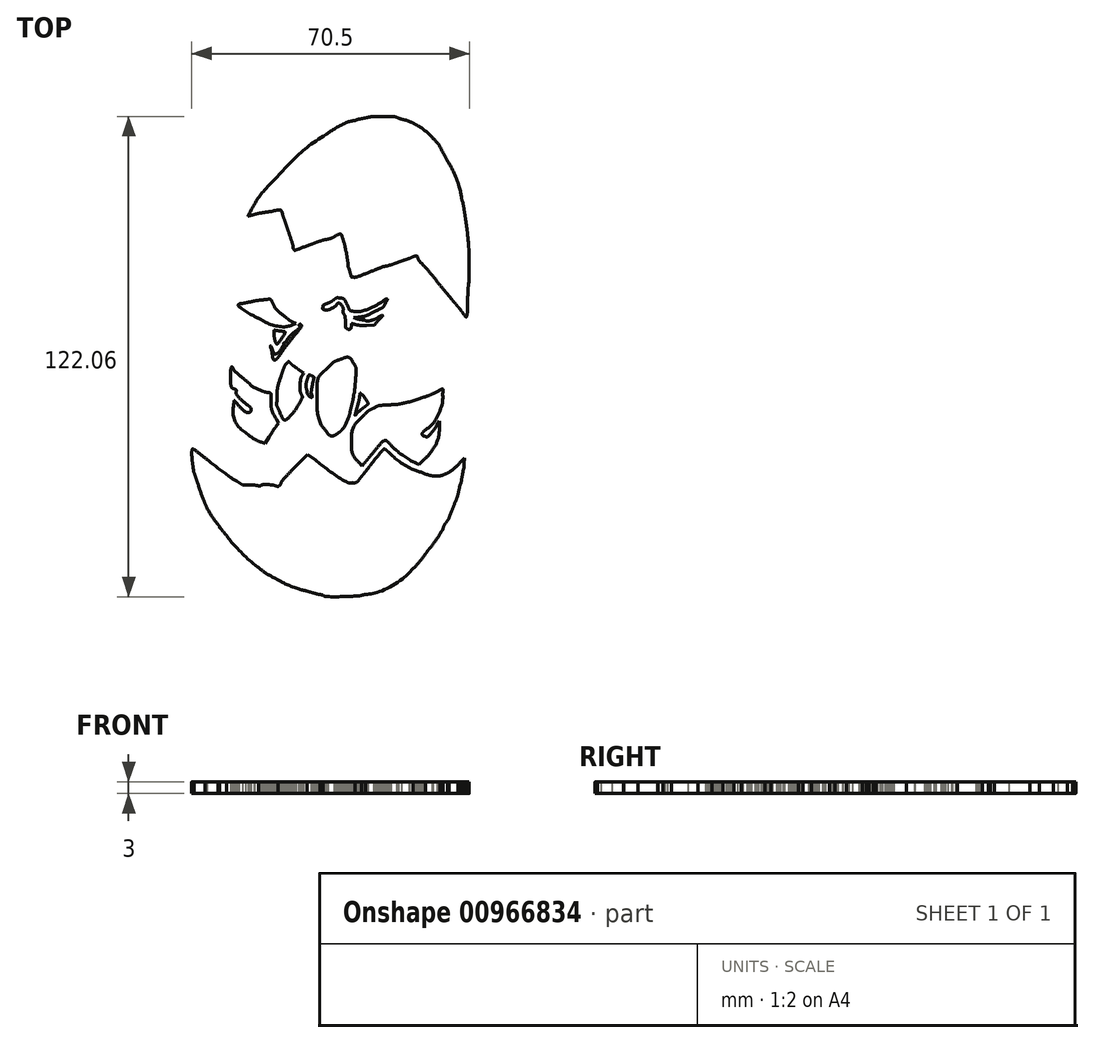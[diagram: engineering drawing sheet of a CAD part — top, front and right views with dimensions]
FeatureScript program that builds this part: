
annotation { "Feature Type Name" : "Feature", "Feature Type Description" : "" }
export const myFeature = defineFeature(function(context is Context, id is Id, definition is map)
    precondition{}
    {
        {
            var Q0;
            Q0=qCreatedBy(makeId("Top.planeOp"),FACE);
            var sketch = newSketch(context, id + "F0", { "sketchPlane" : qUnion([Q0])});
            skLineSegment(sketch, "E0", {"start": v(-17.64, -24.34) * mm, "end": v(-17.4, -23.74) * mm});
            skLineSegment(sketch, "E1", {"start": v(-17.4, -23.74) * mm, "end": v(-18.32, -23.36) * mm});
            skLineSegment(sketch, "E2", {"start": v(-18.63, 27.42) * mm, "end": v(-17.84, 26.76) * mm});
            skLineSegment(sketch, "E3", {"start": v(-17.84, 26.76) * mm, "end": v(-16.9, 28.16) * mm});
            skLineSegment(sketch, "E4", {"start": v(1.09, -62.5) * mm, "end": v(1.09, -62.5) * mm});
            skLineSegment(sketch, "E5", {"start": v(34.01, -27.2) * mm, "end": v(34.13, -25.85) * mm});
            skLineSegment(sketch, "E6", {"start": v(34.13, -25.85) * mm, "end": v(33.12, -26.87) * mm});
            skLineSegment(sketch, "E7", {"start": v(-3.82, -26.37) * mm, "end": v(-5.8, -24.88) * mm});
            skLineSegment(sketch, "E8", {"start": v(-5.8, -24.88) * mm, "end": v(-9, -28.14) * mm});
            skLineSegment(sketch, "E9", {"start": v(-20.55, -32.7) * mm, "end": v(-22.26, -32.68) * mm});
            skLineSegment(sketch, "E10", {"start": v(-22.26, -32.68) * mm, "end": v(-23.8, -31.71) * mm});
            skLineSegment(sketch, "E11", {"start": v(-17.33, -29.73) * mm, "end": v(-17.41, -31.05) * mm});
            skLineSegment(sketch, "E12", {"start": v(-17.41, -31.05) * mm, "end": v(-16.23, -31.1) * mm});
            skLineSegment(sketch, "E13", {"start": v(21.94, -27.16) * mm, "end": v(22.57, -27.45) * mm});
            skLineSegment(sketch, "E14", {"start": v(22.57, -27.45) * mm, "end": v(23.83, -26.21) * mm});
            skLineSegment(sketch, "E15", {"start": v(27.7, -17.94) * mm, "end": v(27.78, -16.4) * mm});
            skLineSegment(sketch, "E16", {"start": v(27.78, -16.4) * mm, "end": v(27.08, -17.43) * mm});
            skLineSegment(sketch, "E17", {"start": v(7.35, -27.02) * mm, "end": v(8.09, -27.86) * mm});
            skLineSegment(sketch, "E18", {"start": v(8.09, -27.86) * mm, "end": v(8.6, -27.2) * mm});
            skLineSegment(sketch, "E19", {"start": v(-13.84, -17.87) * mm, "end": v(-13.14, -16.9) * mm});
            skLineSegment(sketch, "E20", {"start": v(-13.14, -16.9) * mm, "end": v(-13.63, -16.05) * mm});
            skLineSegment(sketch, "E21", {"start": v(-17.2, -21.9) * mm, "end": v(-16.6, -22.1) * mm});
            skLineSegment(sketch, "E22", {"start": v(-16.6, -22.1) * mm, "end": v(-15.58, -20.48) * mm});
            skLineSegment(sketch, "E23", {"start": v(-7, -4.65) * mm, "end": v(-6.75, -4.17) * mm});
            skLineSegment(sketch, "E24", {"start": v(-6.75, -4.17) * mm, "end": v(-8.1, -3.28) * mm});
            skLineSegment(sketch, "E25", {"start": v(29.2, 13.04) * mm, "end": v(29.43, 13.93) * mm});
            skLineSegment(sketch, "E26", {"start": v(29.43, 13.93) * mm, "end": v(28.41, 15.23) * mm});
            skLineSegment(sketch, "E27", {"start": v(1.96, 28.65) * mm, "end": v(1.77, 29.1) * mm});
            skLineSegment(sketch, "E28", {"start": v(1.77, 29.1) * mm, "end": v(0.99, 28.8) * mm});
            skLineSegment(sketch, "E29", {"start": v(-14.89, 28.54) * mm, "end": v(-16.04, 27) * mm});
            skLineSegment(sketch, "E30", {"start": v(-16.04, 27) * mm, "end": v(-15.46, 26.94) * mm});
            skLineSegment(sketch, "E31", {"start": v(-4.31, -3.35) * mm, "end": v(-3.52, -3.65) * mm});
            skLineSegment(sketch, "E32", {"start": v(-3.52, -3.65) * mm, "end": v(-1.91, -2.03) * mm});
            skLineSegment(sketch, "E33", {"start": v(10.44, -4.22) * mm, "end": v(10.44, -4.22) * mm});
            skLineSegment(sketch, "E34", {"start": v(7.03, 10) * mm, "end": v(5.92, 9.88) * mm});
            skLineSegment(sketch, "E35", {"start": v(5.92, 9.88) * mm, "end": v(6.58, 9.65) * mm});
            skLineSegment(sketch, "E36", {"start": v(11.62, 8.44) * mm, "end": v(11.2, 7.9) * mm});
            skLineSegment(sketch, "E37", {"start": v(11.2, 7.9) * mm, "end": v(9.22, 7.89) * mm});
            skLineSegment(sketch, "E38", {"start": v(-9.5, 8.1) * mm, "end": v(-8.74, 8.33) * mm});
            skLineSegment(sketch, "E39", {"start": v(-8.74, 8.33) * mm, "end": v(-9.55, 8.72) * mm});
            skFitSpline(sketch, "E40", {"points": [v(1.09, -62.5) * mm, v(1.07, -62.49) * mm, v(0.46, -62.46) * mm, v(-0.26, -62.44) * mm]});
            skFitSpline(sketch, "E41", {"points": [v(-0.26, -62.44) * mm, v(-1.46, -62.4) * mm, v(-3.84, -62.05) * mm, v(-4.15, -61.86) * mm]});
            skFitSpline(sketch, "E42", {"points": [v(-4.15, -61.86) * mm, v(-4.22, -61.82) * mm, v(-4.46, -61.75) * mm, v(-4.7, -61.7) * mm]});
            skFitSpline(sketch, "E43", {"points": [v(-4.7, -61.7) * mm, v(-4.92, -61.66) * mm, v(-5.61, -61.47) * mm, v(-6.23, -61.27) * mm]});
            skFitSpline(sketch, "E44", {"points": [v(-6.23, -61.27) * mm, v(-6.84, -61.07) * mm, v(-7.52, -60.87) * mm, v(-7.74, -60.83) * mm]});
            skFitSpline(sketch, "E45", {"points": [v(-7.74, -60.83) * mm, v(-8.13, -60.75) * mm, v(-9.97, -60.15) * mm, v(-10.6, -59.88) * mm]});
            skFitSpline(sketch, "E46", {"points": [v(-10.6, -59.88) * mm, v(-10.79, -59.8) * mm, v(-11.21, -59.65) * mm, v(-11.54, -59.53) * mm]});
            skFitSpline(sketch, "E47", {"points": [v(-11.54, -59.53) * mm, v(-12.86, -59.06) * mm, v(-16.51, -57.07) * mm, v(-17.91, -56.06) * mm]});
            skFitSpline(sketch, "E48", {"points": [v(-17.91, -56.06) * mm, v(-20.14, -54.45) * mm, v(-20.57, -54.07) * mm, v(-23.72, -50.89) * mm]});
            skFitSpline(sketch, "E49", {"points": [v(-23.72, -50.89) * mm, v(-26.76, -47.82) * mm, v(-27.5, -47.02) * mm, v(-27.5, -46.8) * mm]});
            skFitSpline(sketch, "E50", {"points": [v(-27.5, -46.8) * mm, v(-27.5, -46.71) * mm, v(-27.87, -46.25) * mm, v(-28.33, -45.76) * mm]});
            skFitSpline(sketch, "E51", {"points": [v(-28.33, -45.76) * mm, v(-29.79, -44.22) * mm, v(-32.43, -40.02) * mm, v(-33.48, -37.57) * mm]});
            skFitSpline(sketch, "E52", {"points": [v(-33.48, -37.57) * mm, v(-33.92, -36.56) * mm, v(-34.68, -34.57) * mm, v(-34.78, -34.15) * mm]});
            skFitSpline(sketch, "E53", {"points": [v(-34.78, -34.15) * mm, v(-34.82, -34) * mm, v(-35.05, -33.32) * mm, v(-35.3, -32.6) * mm]});
            skFitSpline(sketch, "E54", {"points": [v(-35.3, -32.6) * mm, v(-36.32, -29.73) * mm, v(-36.5, -28.65) * mm, v(-36.5, -25.32) * mm]});
            skFitSpline(sketch, "E55", {"points": [v(-36.5, -25.32) * mm, v(-36.5, -22.53) * mm, v(-36.34, -21.27) * mm, v(-35.96, -21) * mm]});
            skFitSpline(sketch, "E56", {"points": [v(-35.96, -21) * mm, v(-35.54, -20.68) * mm, v(-35.42, -20.71) * mm, v(-34.9, -21.26) * mm]});
            skFitSpline(sketch, "E57", {"points": [v(-34.9, -21.26) * mm, v(-34.65, -21.52) * mm, v(-33.59, -22.39) * mm, v(-32.55, -23.18) * mm]});
            skFitSpline(sketch, "E58", {"points": [v(-32.55, -23.18) * mm, v(-31.51, -23.97) * mm, v(-30.63, -24.66) * mm, v(-30.58, -24.71) * mm]});
            skFitSpline(sketch, "E59", {"points": [v(-30.58, -24.71) * mm, v(-30.53, -24.76) * mm, v(-30.19, -25.03) * mm, v(-29.8, -25.3) * mm]});
            skFitSpline(sketch, "E60", {"points": [v(-29.8, -25.3) * mm, v(-29.43, -25.59) * mm, v(-29.08, -25.86) * mm, v(-29.04, -25.92) * mm]});
            skFitSpline(sketch, "E61", {"points": [v(-29.04, -25.92) * mm, v(-28.68, -26.36) * mm, v(-24.52, -29.29) * mm, v(-22.01, -30.85) * mm]});
            skFitSpline(sketch, "E62", {"points": [v(-22.01, -30.85) * mm, v(-21.6, -31.12) * mm, v(-19.15, -31.3) * mm, v(-19.01, -31.08) * mm]});
            skFitSpline(sketch, "E63", {"points": [v(-19.01, -31.08) * mm, v(-18.98, -31.02) * mm, v(-18.9, -30.43) * mm, v(-18.84, -29.77) * mm]});
            skFitSpline(sketch, "E64", {"points": [v(-18.84, -29.77) * mm, v(-18.78, -29.12) * mm, v(-18.7, -28.46) * mm, v(-18.66, -28.32) * mm]});
            skFitSpline(sketch, "E65", {"points": [v(-18.66, -28.32) * mm, v(-18.62, -28.18) * mm, v(-18.54, -27.8) * mm, v(-18.49, -27.46) * mm]});
            skFitSpline(sketch, "E66", {"points": [v(-18.49, -27.46) * mm, v(-18.33, -26.53) * mm, v(-17.92, -25) * mm, v(-17.64, -24.34) * mm]});
            skFitSpline(sketch, "E67", {"points": [v(-18.32, -23.36) * mm, v(-19.44, -22.9) * mm, v(-21.28, -21.62) * mm, v(-22.38, -20.55) * mm]});
            skFitSpline(sketch, "E68", {"points": [v(-22.38, -20.55) * mm, v(-24.7, -18.28) * mm, v(-26.1, -14.85) * mm, v(-25.9, -11.94) * mm]});
            skFitSpline(sketch, "E69", {"points": [v(-25.9, -11.94) * mm, v(-25.84, -11.19) * mm, v(-25.75, -10.37) * mm, v(-25.7, -10.14) * mm]});
            skFitSpline(sketch, "E70", {"points": [v(-25.7, -10.14) * mm, v(-25.64, -9.86) * mm, v(-25.76, -9.39) * mm, v(-26.08, -8.77) * mm]});
            skFitSpline(sketch, "E71", {"points": [v(-26.08, -8.77) * mm, v(-26.54, -7.84) * mm, v(-26.55, -7.77) * mm, v(-26.52, -4.97) * mm]});
            skFitSpline(sketch, "E72", {"points": [v(-26.52, -4.97) * mm, v(-26.5, -2.23) * mm, v(-26.48, -2.09) * mm, v(-26, -1.08) * mm]});
            skFitSpline(sketch, "E73", {"points": [v(-26, -1.08) * mm, v(-25.5, 0.03) * mm, v(-25.26, 0.23) * mm, v(-24.7, 0.05) * mm]});
            skFitSpline(sketch, "E74", {"points": [v(-24.7, 0.05) * mm, v(-24.38, -0.05) * mm, v(-23.44, -1.82) * mm, v(-23.53, -2.16) * mm]});
            skFitSpline(sketch, "E75", {"points": [v(-23.53, -2.16) * mm, v(-23.56, -2.26) * mm, v(-23.52, -2.28) * mm, v(-23.46, -2.22) * mm]});
            skFitSpline(sketch, "E76", {"points": [v(-23.46, -2.22) * mm, v(-23.4, -2.15) * mm, v(-23.1, -2.39) * mm, v(-22.8, -2.73) * mm]});
            skFitSpline(sketch, "E77", {"points": [v(-22.8, -2.73) * mm, v(-21.53, -4.2) * mm, v(-20.04, -5.4) * mm, v(-18.23, -6.4) * mm]});
            skFitSpline(sketch, "E78", {"points": [v(-18.23, -6.4) * mm, v(-17.03, -7.06) * mm, v(-14.86, -7.85) * mm, v(-14.69, -7.68) * mm]});
            skFitSpline(sketch, "E79", {"points": [v(-14.69, -7.68) * mm, v(-14.63, -7.63) * mm, v(-14.52, -7.22) * mm, v(-14.44, -6.77) * mm]});
            skFitSpline(sketch, "E80", {"points": [v(-14.44, -6.77) * mm, v(-14.35, -6.33) * mm, v(-13.98, -5.12) * mm, v(-13.6, -4.1) * mm]});
            skFitSpline(sketch, "E81", {"points": [v(-13.6, -4.1) * mm, v(-13.22, -3.06) * mm, v(-12.91, -2.19) * mm, v(-12.91, -2.14) * mm]});
            skFitSpline(sketch, "E82", {"points": [v(-12.91, -2.14) * mm, v(-12.91, -2.1) * mm, v(-13.06, -2.15) * mm, v(-13.25, -2.24) * mm]});
            skFitSpline(sketch, "E83", {"points": [v(-13.25, -2.24) * mm, v(-13.7, -2.49) * mm, v(-14.83, -2.46) * mm, v(-15.18, -2.18) * mm]});
            skFitSpline(sketch, "E84", {"points": [v(-15.18, -2.18) * mm, v(-15.57, -1.9) * mm, v(-15.94, -1) * mm, v(-16.09, -0.02) * mm]});
            skFitSpline(sketch, "E85", {"points": [v(-16.09, -0.02) * mm, v(-16.15, 0.4) * mm, v(-16.26, 0.86) * mm, v(-16.33, 1) * mm]});
            skFitSpline(sketch, "E86", {"points": [v(-16.33, 1) * mm, v(-16.45, 1.24) * mm, v(-16.58, 1.76) * mm, v(-16.8, 2.98) * mm]});
            skFitSpline(sketch, "E87", {"points": [v(-16.8, 2.98) * mm, v(-16.84, 3.17) * mm, v(-16.94, 3.6) * mm, v(-17.03, 3.93) * mm]});
            skFitSpline(sketch, "E88", {"points": [v(-17.03, 3.93) * mm, v(-17.11, 4.26) * mm, v(-17.23, 4.91) * mm, v(-17.28, 5.38) * mm]});
            skFitSpline(sketch, "E89", {"points": [v(-17.28, 5.38) * mm, v(-17.52, 7.42) * mm, v(-17.6, 7.56) * mm, v(-19.14, 8.38) * mm]});
            skFitSpline(sketch, "E90", {"points": [v(-19.14, 8.38) * mm, v(-21.39, 9.58) * mm, v(-22.76, 10.52) * mm, v(-23.65, 11.48) * mm]});
            skFitSpline(sketch, "E91", {"points": [v(-23.65, 11.48) * mm, v(-24.11, 11.97) * mm, v(-24.74, 12.6) * mm, v(-25.05, 12.9) * mm]});
            skFitSpline(sketch, "E92", {"points": [v(-25.05, 12.9) * mm, v(-25.6, 13.41) * mm, v(-25.74, 13.91) * mm, v(-25.46, 14.35) * mm]});
            skFitSpline(sketch, "E93", {"points": [v(-25.46, 14.35) * mm, v(-25.39, 14.46) * mm, v(-24.68, 14.64) * mm, v(-23.88, 14.73) * mm]});
            skFitSpline(sketch, "E94", {"points": [v(-23.88, 14.73) * mm, v(-20.97, 15.08) * mm, v(-20.33, 15.2) * mm, v(-20.16, 15.48) * mm]});
            skFitSpline(sketch, "E95", {"points": [v(-20.16, 15.48) * mm, v(-20.1, 15.59) * mm, v(-20.03, 16.45) * mm, v(-20.02, 17.39) * mm]});
            skFitSpline(sketch, "E96", {"points": [v(-20.02, 17.39) * mm, v(-20.01, 18.33) * mm, v(-19.94, 19.41) * mm, v(-19.87, 19.8) * mm]});
            skFitSpline(sketch, "E97", {"points": [v(-19.87, 19.8) * mm, v(-19.7, 20.59) * mm, v(-19.65, 20.93) * mm, v(-19.52, 21.8) * mm]});
            skFitSpline(sketch, "E98", {"points": [v(-19.52, 21.8) * mm, v(-19.47, 22.16) * mm, v(-19.27, 22.84) * mm, v(-19.08, 23.33) * mm]});
            skFitSpline(sketch, "E99", {"points": [v(-19.08, 23.33) * mm, v(-18.89, 23.81) * mm, v(-18.76, 24.24) * mm, v(-18.8, 24.28) * mm]});
            skFitSpline(sketch, "E100", {"points": [v(-18.8, 24.28) * mm, v(-18.84, 24.32) * mm, v(-19.05, 24.38) * mm, v(-19.28, 24.42) * mm]});
            skFitSpline(sketch, "E101", {"points": [v(-19.28, 24.42) * mm, v(-20.48, 24.65) * mm, v(-20.79, 24.73) * mm, v(-21.54, 24.97) * mm]});
            skFitSpline(sketch, "E102", {"points": [v(-21.54, 24.97) * mm, v(-22.34, 25.22) * mm, v(-22.36, 25.24) * mm, v(-22.31, 25.85) * mm]});
            skFitSpline(sketch, "E103", {"points": [v(-22.31, 25.85) * mm, v(-22.27, 26.4) * mm, v(-22.2, 26.48) * mm, v(-21.83, 26.48) * mm]});
            skFitSpline(sketch, "E104", {"points": [v(-21.83, 26.48) * mm, v(-21.6, 26.47) * mm, v(-21.03, 26.37) * mm, v(-20.58, 26.24) * mm]});
            skFitSpline(sketch, "E105", {"points": [v(-20.58, 26.24) * mm, v(-19.65, 25.97) * mm, v(-19.39, 26.08) * mm, v(-19.89, 26.52) * mm]});
            skFitSpline(sketch, "E106", {"points": [v(-19.89, 26.52) * mm, v(-20.48, 27.04) * mm, v(-21.49, 28.46) * mm, v(-21.49, 28.78) * mm]});
            skFitSpline(sketch, "E107", {"points": [v(-21.49, 28.78) * mm, v(-21.49, 28.94) * mm, v(-21.38, 29.22) * mm, v(-21.24, 29.4) * mm]});
            skFitSpline(sketch, "E108", {"points": [v(-21.24, 29.4) * mm, v(-21, 29.73) * mm, v(-20.96, 29.7) * mm, v(-20.2, 28.9) * mm]});
            skFitSpline(sketch, "E109", {"points": [v(-20.2, 28.9) * mm, v(-19.78, 28.45) * mm, v(-19.07, 27.78) * mm, v(-18.63, 27.42) * mm]});
            skFitSpline(sketch, "E110", {"points": [v(-16.9, 28.16) * mm, v(-15.9, 29.64) * mm, v(-14.7, 31.14) * mm, v(-13.47, 32.36) * mm]});
            skFitSpline(sketch, "E111", {"points": [v(-13.47, 32.36) * mm, v(-13.07, 32.77) * mm, v(-12.74, 33.2) * mm, v(-12.74, 33.33) * mm]});
            skFitSpline(sketch, "E112", {"points": [v(-12.74, 33.33) * mm, v(-12.74, 33.45) * mm, v(-12.94, 34) * mm, v(-13.18, 34.54) * mm]});
            skFitSpline(sketch, "E113", {"points": [v(-13.18, 34.54) * mm, v(-13.6, 35.5) * mm, v(-13.63, 35.52) * mm, v(-14.16, 35.42) * mm]});
            skFitSpline(sketch, "E114", {"points": [v(-14.16, 35.42) * mm, v(-14.47, 35.36) * mm, v(-15.06, 35.27) * mm, v(-15.49, 35.21) * mm]});
            skFitSpline(sketch, "E115", {"points": [v(-15.49, 35.21) * mm, v(-17.01, 35.02) * mm, v(-19.02, 34.64) * mm, v(-19.86, 34.39) * mm]});
            skFitSpline(sketch, "E116", {"points": [v(-19.86, 34.39) * mm, v(-20.33, 34.25) * mm, v(-20.98, 34.1) * mm, v(-21.3, 34.05) * mm]});
            skFitSpline(sketch, "E117", {"points": [v(-21.3, 34.05) * mm, v(-21.62, 34) * mm, v(-21.96, 33.88) * mm, v(-22.06, 33.78) * mm]});
            skFitSpline(sketch, "E118", {"points": [v(-22.06, 33.78) * mm, v(-22.16, 33.68) * mm, v(-22.41, 33.6) * mm, v(-22.62, 33.6) * mm]});
            skFitSpline(sketch, "E119", {"points": [v(-22.62, 33.6) * mm, v(-23.45, 33.6) * mm, v(-23.52, 34.51) * mm, v(-22.77, 35.72) * mm]});
            skFitSpline(sketch, "E120", {"points": [v(-22.77, 35.72) * mm, v(-19.1, 41.6) * mm, v(-18.03, 43.06) * mm, v(-15.74, 45.35) * mm]});
            skFitSpline(sketch, "E121", {"points": [v(-15.74, 45.35) * mm, v(-11.87, 49.2) * mm, v(-7.67, 53.23) * mm, v(-6.65, 54.1) * mm]});
            skFitSpline(sketch, "E122", {"points": [v(-6.65, 54.1) * mm, v(-6.09, 54.57) * mm, v(-5.48, 55.09) * mm, v(-5.3, 55.25) * mm]});
            skFitSpline(sketch, "E123", {"points": [v(-5.3, 55.25) * mm, v(-5.12, 55.41) * mm, v(-4.65, 55.76) * mm, v(-4.27, 56.02) * mm]});
            skFitSpline(sketch, "E124", {"points": [v(-4.27, 56.02) * mm, v(-3.88, 56.28) * mm, v(-3.53, 56.54) * mm, v(-3.48, 56.6) * mm]});
            skFitSpline(sketch, "E125", {"points": [v(-3.48, 56.6) * mm, v(-3.18, 56.94) * mm, v(-0.95, 58.3) * mm, v(1, 59.31) * mm]});
            skFitSpline(sketch, "E126", {"points": [v(1, 59.31) * mm, v(3, 60.36) * mm, v(6, 61.53) * mm, v(7.33, 61.8) * mm]});
            skFitSpline(sketch, "E127", {"points": [v(7.33, 61.8) * mm, v(10.1, 62.34) * mm, v(10.94, 62.44) * mm, v(13.33, 62.5) * mm]});
            skFitSpline(sketch, "E128", {"points": [v(13.33, 62.5) * mm, v(15.91, 62.56) * mm, v(17.13, 62.4) * mm, v(19.1, 61.74) * mm]});
            skFitSpline(sketch, "E129", {"points": [v(19.1, 61.74) * mm, v(22.69, 60.54) * mm, v(26.05, 58.26) * mm, v(27.97, 55.74) * mm]});
            skFitSpline(sketch, "E130", {"points": [v(27.97, 55.74) * mm, v(29.06, 54.31) * mm, v(30.31, 52.15) * mm, v(31.72, 49.27) * mm]});
            skFitSpline(sketch, "E131", {"points": [v(31.72, 49.27) * mm, v(33.14, 46.38) * mm, v(33.63, 45.02) * mm, v(34.5, 41.57) * mm]});
            skFitSpline(sketch, "E132", {"points": [v(34.5, 41.57) * mm, v(35.22, 38.77) * mm, v(35.23, 38.75) * mm, v(35.54, 36.43) * mm]});
            skFitSpline(sketch, "E133", {"points": [v(35.54, 36.43) * mm, v(35.58, 36.15) * mm, v(35.64, 35.76) * mm, v(35.68, 35.57) * mm]});
            skFitSpline(sketch, "E134", {"points": [v(35.68, 35.57) * mm, v(35.73, 35.38) * mm, v(35.81, 34.65) * mm, v(35.88, 33.94) * mm]});
            skFitSpline(sketch, "E135", {"points": [v(35.88, 33.94) * mm, v(35.94, 33.23) * mm, v(36.02, 32.46) * mm, v(36.05, 32.23) * mm]});
            skFitSpline(sketch, "E136", {"points": [v(36.05, 32.23) * mm, v(36.24, 30.91) * mm, v(36.36, 29.83) * mm, v(36.41, 29.06) * mm]});
            skFitSpline(sketch, "E137", {"points": [v(36.41, 29.06) * mm, v(36.5, 27.7) * mm, v(36.5, 19.13) * mm, v(36.4, 17.22) * mm]});
            skFitSpline(sketch, "E138", {"points": [v(36.4, 17.22) * mm, v(36.35, 16.27) * mm, v(36.28, 14.54) * mm, v(36.24, 13.36) * mm]});
            skFitSpline(sketch, "E139", {"points": [v(36.24, 13.36) * mm, v(36.2, 12.18) * mm, v(36.14, 10.94) * mm, v(36.08, 10.61) * mm]});
            skFitSpline(sketch, "E140", {"points": [v(36.08, 10.61) * mm, v(36.03, 10.28) * mm, v(35.97, 9.42) * mm, v(35.95, 8.7) * mm]});
            skFitSpline(sketch, "E141", {"points": [v(35.95, 8.7) * mm, v(35.9, 7.22) * mm, v(35.76, 7.03) * mm, v(34.78, 7.16) * mm]});
            skFitSpline(sketch, "E142", {"points": [v(34.78, 7.16) * mm, v(34.69, 7.18) * mm, v(34.36, 7.55) * mm, v(34.06, 8) * mm]});
            skFitSpline(sketch, "E143", {"points": [v(34.06, 8) * mm, v(33.1, 9.4) * mm, v(30.96, 12.07) * mm, v(30.76, 12.1) * mm]});
            skFitSpline(sketch, "E144", {"points": [v(30.76, 12.1) * mm, v(30.65, 12.13) * mm, v(30.27, 11.52) * mm, v(29.9, 10.75) * mm]});
            skFitSpline(sketch, "E145", {"points": [v(29.9, 10.75) * mm, v(29.33, 9.57) * mm, v(27.59, 6.78) * mm, v(27.24, 6.5) * mm]});
            skFitSpline(sketch, "E146", {"points": [v(27.24, 6.5) * mm, v(27.18, 6.45) * mm, v(26.87, 6.07) * mm, v(26.54, 5.64) * mm]});
            skFitSpline(sketch, "E147", {"points": [v(26.54, 5.64) * mm, v(24.96, 3.59) * mm, v(21.88, 0.6) * mm, v(19.59, -1.12) * mm]});
            skFitSpline(sketch, "E148", {"points": [v(19.59, -1.12) * mm, v(15.64, -4.08) * mm, v(12.52, -5.52) * mm, v(8.8, -6.1) * mm]});
            skFitSpline(sketch, "E149", {"points": [v(8.8, -6.1) * mm, v(7.97, -6.23) * mm, v(7.9, -6.27) * mm, v(7.8, -6.78) * mm]});
            skFitSpline(sketch, "E150", {"points": [v(7.8, -6.78) * mm, v(7.74, -7.1) * mm, v(7.92, -7.38) * mm, v(8.65, -8.1) * mm]});
            skFitSpline(sketch, "E151", {"points": [v(8.65, -8.1) * mm, v(9.16, -8.6) * mm, v(9.93, -9.54) * mm, v(10.36, -10.18) * mm]});
            skFitSpline(sketch, "E152", {"points": [v(10.36, -10.18) * mm, v(11.19, -11.43) * mm, v(11.13, -11.4) * mm, v(12.47, -11.1) * mm]});
            skFitSpline(sketch, "E153", {"points": [v(12.47, -11.1) * mm, v(12.7, -11.06) * mm, v(13.71, -10.97) * mm, v(14.7, -10.91) * mm]});
            skFitSpline(sketch, "E154", {"points": [v(14.7, -10.91) * mm, v(15.7, -10.86) * mm, v(16.7, -10.79) * mm, v(16.93, -10.76) * mm]});
            skFitSpline(sketch, "E155", {"points": [v(16.93, -10.76) * mm, v(18.33, -10.57) * mm, v(19.12, -10.42) * mm, v(19.5, -10.27) * mm]});
            skFitSpline(sketch, "E156", {"points": [v(19.5, -10.27) * mm, v(19.74, -10.18) * mm, v(20.05, -10.08) * mm, v(20.19, -10.05) * mm]});
            skFitSpline(sketch, "E157", {"points": [v(20.19, -10.05) * mm, v(20.67, -9.95) * mm, v(24.21, -8.65) * mm, v(25.5, -8.1) * mm]});
            skFitSpline(sketch, "E158", {"points": [v(25.5, -8.1) * mm, v(26.21, -7.8) * mm, v(27.32, -7.22) * mm, v(27.97, -6.8) * mm]});
            skFitSpline(sketch, "E159", {"points": [v(27.97, -6.8) * mm, v(29, -6.14) * mm, v(29.2, -6.07) * mm, v(29.56, -6.24) * mm]});
            skFitSpline(sketch, "E160", {"points": [v(29.56, -6.24) * mm, v(30.1, -6.48) * mm, v(30.2, -6.94) * mm, v(30.1, -8.74) * mm]});
            skFitSpline(sketch, "E161", {"points": [v(30.1, -8.74) * mm, v(30, -10.44) * mm, v(30.06, -10.14) * mm, v(29.27, -12.55) * mm]});
            skFitSpline(sketch, "E162", {"points": [v(29.27, -12.55) * mm, v(28.87, -13.79) * mm, v(28.7, -14.53) * mm, v(28.8, -14.76) * mm]});
            skFitSpline(sketch, "E163", {"points": [v(28.8, -14.76) * mm, v(29.24, -15.96) * mm, v(29.26, -18.35) * mm, v(28.85, -19.86) * mm]});
            skFitSpline(sketch, "E164", {"points": [v(28.85, -19.86) * mm, v(28.7, -20.4) * mm, v(28.54, -21.05) * mm, v(28.5, -21.29) * mm]});
            skFitSpline(sketch, "E165", {"points": [v(28.5, -21.29) * mm, v(28.34, -22.03) * mm, v(26.93, -24.78) * mm, v(26.2, -25.75) * mm]});
            skFitSpline(sketch, "E166", {"points": [v(26.2, -25.75) * mm, v(25.83, -26.26) * mm, v(25.23, -26.97) * mm, v(24.89, -27.33) * mm]});
            skFitSpline(sketch, "E167", {"points": [v(24.89, -27.33) * mm, v(24.54, -27.7) * mm, v(24.3, -28.01) * mm, v(24.33, -28.04) * mm]});
            skFitSpline(sketch, "E168", {"points": [v(24.33, -28.04) * mm, v(24.63, -28.3) * mm, v(25.74, -28.46) * mm, v(27.03, -28.45) * mm]});
            skFitSpline(sketch, "E169", {"points": [v(27.03, -28.45) * mm, v(28.4, -28.45) * mm, v(28.66, -28.4) * mm, v(29.23, -28) * mm]});
            skFitSpline(sketch, "E170", {"points": [v(29.23, -28) * mm, v(29.59, -27.77) * mm, v(29.92, -27.52) * mm, v(29.97, -27.46) * mm]});
            skFitSpline(sketch, "E171", {"points": [v(29.97, -27.46) * mm, v(30.01, -27.4) * mm, v(30.4, -27.12) * mm, v(30.82, -26.82) * mm]});
            skFitSpline(sketch, "E172", {"points": [v(30.82, -26.82) * mm, v(31.62, -26.28) * mm, v(32.09, -25.86) * mm, v(32.54, -25.3) * mm]});
            skFitSpline(sketch, "E173", {"points": [v(32.54, -25.3) * mm, v(34, -23.47) * mm, v(34.13, -23.35) * mm, v(34.6, -23.35) * mm]});
            skFitSpline(sketch, "E174", {"points": [v(34.6, -23.35) * mm, v(35.38, -23.35) * mm, v(35.6, -23.85) * mm, v(35.53, -25.38) * mm]});
            skFitSpline(sketch, "E175", {"points": [v(35.53, -25.38) * mm, v(35.44, -27.26) * mm, v(35.28, -29.4) * mm, v(35.2, -29.88) * mm]});
            skFitSpline(sketch, "E176", {"points": [v(35.2, -29.88) * mm, v(34.94, -31.27) * mm, v(34.17, -34.45) * mm, v(33.79, -35.7) * mm]});
            skFitSpline(sketch, "E177", {"points": [v(33.79, -35.7) * mm, v(33.54, -36.5) * mm, v(33.32, -37.2) * mm, v(33.3, -37.24) * mm]});
            skFitSpline(sketch, "E178", {"points": [v(33.3, -37.24) * mm, v(33.27, -37.36) * mm, v(33.13, -37.71) * mm, v(32.18, -39.98) * mm]});
            skFitSpline(sketch, "E179", {"points": [v(32.18, -39.98) * mm, v(30.62, -43.74) * mm, v(28.83, -46.64) * mm, v(24.64, -52.16) * mm]});
            skFitSpline(sketch, "E180", {"points": [v(24.64, -52.16) * mm, v(22.7, -54.71) * mm, v(19.18, -57.65) * mm, v(16.17, -59.22) * mm]});
            skFitSpline(sketch, "E181", {"points": [v(16.17, -59.22) * mm, v(15.6, -59.51) * mm, v(14.94, -59.9) * mm, v(14.7, -60.06) * mm]});
            skFitSpline(sketch, "E182", {"points": [v(14.7, -60.06) * mm, v(13.95, -60.6) * mm, v(10.54, -61.78) * mm, v(9.04, -62.02) * mm]});
            skFitSpline(sketch, "E183", {"points": [v(9.04, -62.02) * mm, v(8.71, -62.07) * mm, v(8.25, -62.15) * mm, v(8.01, -62.2) * mm]});
            skFitSpline(sketch, "E184", {"points": [v(8.01, -62.2) * mm, v(6.66, -62.44) * mm, v(5.8, -62.5) * mm, v(3.58, -62.52) * mm]});
            skFitSpline(sketch, "E185", {"points": [v(3.58, -62.52) * mm, v(2.23, -62.53) * mm, v(1.1, -62.52) * mm, v(1.09, -62.5) * mm]});
            skFitSpline(sketch, "E186", {"points": [v(6.3, -60.9) * mm, v(6.9, -60.87) * mm, v(7.64, -60.79) * mm, v(7.93, -60.7) * mm]});
            skFitSpline(sketch, "E187", {"points": [v(7.93, -60.7) * mm, v(8.2, -60.63) * mm, v(8.67, -60.52) * mm, v(8.96, -60.47) * mm]});
            skFitSpline(sketch, "E188", {"points": [v(8.96, -60.47) * mm, v(12.18, -59.89) * mm, v(18.29, -56.56) * mm, v(21, -53.92) * mm]});
            skFitSpline(sketch, "E189", {"points": [v(21, -53.92) * mm, v(21.82, -53.1) * mm, v(23.17, -51.51) * mm, v(24.15, -50.2) * mm]});
            skFitSpline(sketch, "E190", {"points": [v(24.15, -50.2) * mm, v(24.56, -49.63) * mm, v(25, -49.05) * mm, v(25.11, -48.9) * mm]});
            skFitSpline(sketch, "E191", {"points": [v(25.11, -48.9) * mm, v(26.02, -47.75) * mm, v(27.56, -45.62) * mm, v(27.83, -45.13) * mm]});
            skFitSpline(sketch, "E192", {"points": [v(27.83, -45.13) * mm, v(28.01, -44.8) * mm, v(28.25, -44.41) * mm, v(28.37, -44.27) * mm]});
            skFitSpline(sketch, "E193", {"points": [v(28.37, -44.27) * mm, v(28.48, -44.13) * mm, v(28.58, -43.94) * mm, v(28.6, -43.84) * mm]});
            skFitSpline(sketch, "E194", {"points": [v(28.6, -43.84) * mm, v(28.66, -43.52) * mm, v(29.32, -42.3) * mm, v(29.73, -41.75) * mm]});
            skFitSpline(sketch, "E195", {"points": [v(29.73, -41.75) * mm, v(29.95, -41.45) * mm, v(30.14, -41.15) * mm, v(30.14, -41.1) * mm]});
            skFitSpline(sketch, "E196", {"points": [v(30.14, -41.1) * mm, v(30.14, -41.03) * mm, v(30.64, -39.73) * mm, v(31.24, -38.2) * mm]});
            skFitSpline(sketch, "E197", {"points": [v(31.24, -38.2) * mm, v(31.85, -36.68) * mm, v(32.39, -35.24) * mm, v(32.44, -35) * mm]});
            skFitSpline(sketch, "E198", {"points": [v(32.44, -35) * mm, v(32.79, -33.37) * mm, v(33.01, -32.47) * mm, v(33.1, -32.31) * mm]});
            skFitSpline(sketch, "E199", {"points": [v(33.1, -32.31) * mm, v(33.17, -32.21) * mm, v(33.26, -31.83) * mm, v(33.31, -31.47) * mm]});
            skFitSpline(sketch, "E200", {"points": [v(33.31, -31.47) * mm, v(33.36, -31.1) * mm, v(33.44, -30.64) * mm, v(33.48, -30.45) * mm]});
            skFitSpline(sketch, "E201", {"points": [v(33.48, -30.45) * mm, v(33.53, -30.25) * mm, v(33.6, -29.78) * mm, v(33.67, -29.42) * mm]});
            skFitSpline(sketch, "E202", {"points": [v(33.67, -29.42) * mm, v(33.73, -29.05) * mm, v(33.8, -28.7) * mm, v(33.84, -28.65) * mm]});
            skFitSpline(sketch, "E203", {"points": [v(33.84, -28.65) * mm, v(33.87, -28.59) * mm, v(33.95, -27.94) * mm, v(34.01, -27.2) * mm]});
            skFitSpline(sketch, "E204", {"points": [v(33.12, -26.87) * mm, v(31.95, -28.06) * mm, v(30.18, -29.45) * mm, v(29.5, -29.71) * mm]});
            skFitSpline(sketch, "E205", {"points": [v(29.5, -29.71) * mm, v(27.93, -30.33) * mm, v(25.28, -30.2) * mm, v(22.97, -29.42) * mm]});
            skFitSpline(sketch, "E206", {"points": [v(22.97, -29.42) * mm, v(20.82, -28.68) * mm, v(16.86, -26.23) * mm, v(14.78, -24.33) * mm]});
            skFitSpline(sketch, "E207", {"points": [v(14.78, -24.33) * mm, v(14.28, -23.88) * mm, v(13.81, -23.52) * mm, v(13.73, -23.52) * mm]});
            skFitSpline(sketch, "E208", {"points": [v(13.73, -23.52) * mm, v(13.6, -23.52) * mm, v(13, -24.16) * mm, v(11.6, -25.82) * mm]});
            skFitSpline(sketch, "E209", {"points": [v(11.6, -25.82) * mm, v(11.36, -26.11) * mm, v(10.52, -27.2) * mm, v(9.72, -28.23) * mm]});
            skFitSpline(sketch, "E210", {"points": [v(9.72, -28.23) * mm, v(8.93, -29.27) * mm, v(8.24, -30.16) * mm, v(8.18, -30.2) * mm]});
            skFitSpline(sketch, "E211", {"points": [v(8.18, -30.2) * mm, v(8.13, -30.25) * mm, v(7.86, -30.59) * mm, v(7.59, -30.95) * mm]});
            skFitSpline(sketch, "E212", {"points": [v(7.59, -30.95) * mm, v(7.05, -31.67) * mm, v(6.36, -32.1) * mm, v(5.73, -32.1) * mm]});
            skFitSpline(sketch, "E213", {"points": [v(5.73, -32.1) * mm, v(4.68, -32.1) * mm, v(0.2, -29.41) * mm, v(-3.82, -26.37) * mm]});
            skFitSpline(sketch, "E214", {"points": [v(-9, -28.14) * mm, v(-10.75, -29.94) * mm, v(-12.31, -31.67) * mm, v(-12.47, -32) * mm]});
            skFitSpline(sketch, "E215", {"points": [v(-12.47, -32) * mm, v(-12.83, -32.76) * mm, v(-13.29, -33.01) * mm, v(-14, -32.85) * mm]});
            skFitSpline(sketch, "E216", {"points": [v(-14, -32.85) * mm, v(-14.8, -32.66) * mm, v(-17.43, -32.64) * mm, v(-17.67, -32.83) * mm]});
            skFitSpline(sketch, "E217", {"points": [v(-17.67, -32.83) * mm, v(-17.79, -32.92) * mm, v(-18.1, -32.93) * mm, v(-18.36, -32.86) * mm]});
            skFitSpline(sketch, "E218", {"points": [v(-18.36, -32.86) * mm, v(-18.62, -32.78) * mm, v(-19.6, -32.71) * mm, v(-20.55, -32.7) * mm]});
            skFitSpline(sketch, "E219", {"points": [v(-23.8, -31.71) * mm, v(-25.35, -30.75) * mm, v(-28.18, -28.68) * mm, v(-31.33, -26.2) * mm]});
            skFitSpline(sketch, "E220", {"points": [v(-31.33, -26.2) * mm, v(-33.75, -24.3) * mm, v(-35, -23.48) * mm, v(-35.08, -23.74) * mm]});
            skFitSpline(sketch, "E221", {"points": [v(-35.08, -23.74) * mm, v(-35.19, -24.06) * mm, v(-35.12, -26.22) * mm, v(-34.95, -27.55) * mm]});
            skFitSpline(sketch, "E222", {"points": [v(-34.95, -27.55) * mm, v(-34.87, -28.2) * mm, v(-34.79, -28.86) * mm, v(-34.78, -29) * mm]});
            skFitSpline(sketch, "E223", {"points": [v(-34.78, -29) * mm, v(-34.76, -29.15) * mm, v(-34.7, -29.38) * mm, v(-34.64, -29.52) * mm]});
            skFitSpline(sketch, "E224", {"points": [v(-34.64, -29.52) * mm, v(-34.59, -29.66) * mm, v(-34.04, -31.25) * mm, v(-33.43, -33.05) * mm]});
            skFitSpline(sketch, "E225", {"points": [v(-33.43, -33.05) * mm, v(-32.81, -34.86) * mm, v(-32.08, -36.85) * mm, v(-31.79, -37.48) * mm]});
            skFitSpline(sketch, "E226", {"points": [v(-31.79, -37.48) * mm, v(-31.18, -38.8) * mm, v(-29.44, -41.62) * mm, v(-28.58, -42.68) * mm]});
            skFitSpline(sketch, "E227", {"points": [v(-28.58, -42.68) * mm, v(-28.25, -43.09) * mm, v(-28.05, -43.41) * mm, v(-28.12, -43.42) * mm]});
            skFitSpline(sketch, "E228", {"points": [v(-28.12, -43.42) * mm, v(-28.2, -43.42) * mm, v(-28.19, -43.47) * mm, v(-28.09, -43.54) * mm]});
            skFitSpline(sketch, "E229", {"points": [v(-28.09, -43.54) * mm, v(-28, -43.61) * mm, v(-27.22, -44.52) * mm, v(-26.38, -45.56) * mm]});
            skFitSpline(sketch, "E230", {"points": [v(-26.38, -45.56) * mm, v(-24.37, -48.02) * mm, v(-20.48, -51.88) * mm, v(-18.18, -53.69) * mm]});
            skFitSpline(sketch, "E231", {"points": [v(-18.18, -53.69) * mm, v(-16.44, -55.06) * mm, v(-15.93, -55.38) * mm, v(-13.25, -56.82) * mm]});
            skFitSpline(sketch, "E232", {"points": [v(-13.25, -56.82) * mm, v(-11.62, -57.7) * mm, v(-7.96, -59.11) * mm, v(-5.97, -59.64) * mm]});
            skFitSpline(sketch, "E233", {"points": [v(-5.97, -59.64) * mm, v(-5.87, -59.66) * mm, v(-5.23, -59.84) * mm, v(-4.55, -60.04) * mm]});
            skFitSpline(sketch, "E234", {"points": [v(-4.55, -60.04) * mm, v(-3.86, -60.24) * mm, v(-3.01, -60.44) * mm, v(-2.66, -60.5) * mm]});
            skFitSpline(sketch, "E235", {"points": [v(-2.66, -60.5) * mm, v(-2.31, -60.55) * mm, v(-1.95, -60.64) * mm, v(-1.87, -60.7) * mm]});
            skFitSpline(sketch, "E236", {"points": [v(-1.87, -60.7) * mm, v(-1.5, -60.92) * mm, v(3.02, -61.04) * mm, v(6.3, -60.9) * mm]});
            skFitSpline(sketch, "E237", {"points": [v(-12.68, -29.84) * mm, v(-12.02, -29.15) * mm, v(-10.7, -27.76) * mm, v(-9.75, -26.77) * mm]});
            skFitSpline(sketch, "E238", {"points": [v(-9.75, -26.77) * mm, v(-8.8, -25.77) * mm, v(-7.55, -24.44) * mm, v(-6.97, -23.8) * mm]});
            skFitSpline(sketch, "E239", {"points": [v(-6.97, -23.8) * mm, v(-5.97, -22.7) * mm, v(-5.9, -22.66) * mm, v(-5.47, -22.85) * mm]});
            skFitSpline(sketch, "E240", {"points": [v(-5.47, -22.85) * mm, v(-5.23, -22.97) * mm, v(-5.02, -23.12) * mm, v(-5.02, -23.2) * mm]});
            skFitSpline(sketch, "E241", {"points": [v(-5.02, -23.2) * mm, v(-5.02, -23.26) * mm, v(-4.27, -23.89) * mm, v(-3.35, -24.58) * mm]});
            skFitSpline(sketch, "E242", {"points": [v(-3.35, -24.58) * mm, v(-2.43, -25.27) * mm, v(-1.64, -25.87) * mm, v(-1.6, -25.92) * mm]});
            skFitSpline(sketch, "E243", {"points": [v(-1.6, -25.92) * mm, v(-1.55, -25.98) * mm, v(-1.24, -26.2) * mm, v(-0.9, -26.43) * mm]});
            skFitSpline(sketch, "E244", {"points": [v(-0.9, -26.43) * mm, v(-0.58, -26.66) * mm, v(-0.27, -26.89) * mm, v(-0.22, -26.94) * mm]});
            skFitSpline(sketch, "E245", {"points": [v(-0.22, -26.94) * mm, v(0.16, -27.4) * mm, v(3.85, -29.55) * mm, v(5.14, -30.1) * mm]});
            skFitSpline(sketch, "E246", {"points": [v(5.14, -30.1) * mm, v(5.76, -30.35) * mm, v(5.8, -30.35) * mm, v(6.3, -29.92) * mm]});
            skFitSpline(sketch, "E247", {"points": [v(6.3, -29.92) * mm, v(6.58, -29.69) * mm, v(6.81, -29.41) * mm, v(6.81, -29.32) * mm]});
            skFitSpline(sketch, "E248", {"points": [v(6.81, -29.32) * mm, v(6.81, -29.22) * mm, v(6.52, -28.81) * mm, v(6.17, -28.4) * mm]});
            skFitSpline(sketch, "E249", {"points": [v(6.17, -28.4) * mm, v(5.81, -28) * mm, v(5.31, -27.26) * mm, v(5.05, -26.75) * mm]});
            skFitSpline(sketch, "E250", {"points": [v(5.05, -26.75) * mm, v(4.58, -25.82) * mm, v(4.03, -24.37) * mm, v(4.15, -24.37) * mm]});
            skFitSpline(sketch, "E251", {"points": [v(4.15, -24.37) * mm, v(4.18, -24.37) * mm, v(4.14, -24.12) * mm, v(4.05, -23.82) * mm]});
            skFitSpline(sketch, "E252", {"points": [v(4.05, -23.82) * mm, v(3.86, -23.17) * mm, v(3.82, -20.48) * mm, v(4, -20) * mm]});
            skFitSpline(sketch, "E253", {"points": [v(4, -20) * mm, v(4.08, -19.76) * mm, v(3.9, -19.85) * mm, v(3.45, -20.28) * mm]});
            skFitSpline(sketch, "E254", {"points": [v(3.45, -20.28) * mm, v(2.48, -21.19) * mm, v(2.19, -21.29) * mm, v(0.56, -21.29) * mm]});
            skFitSpline(sketch, "E255", {"points": [v(0.56, -21.29) * mm, v(-0.88, -21.29) * mm, v(-0.92, -21.28) * mm, v(-1.58, -20.68) * mm]});
            skFitSpline(sketch, "E256", {"points": [v(-1.58, -20.68) * mm, v(-1.95, -20.34) * mm, v(-2.5, -19.59) * mm, v(-2.78, -19) * mm]});
            skFitSpline(sketch, "E257", {"points": [v(-2.78, -19) * mm, v(-3.58, -17.4) * mm, v(-4.48, -14.45) * mm, v(-4.6, -13.03) * mm]});
            skFitSpline(sketch, "E258", {"points": [v(-4.6, -13.03) * mm, v(-4.67, -12.34) * mm, v(-4.79, -11.7) * mm, v(-4.87, -11.6) * mm]});
            skFitSpline(sketch, "E259", {"points": [v(-4.87, -11.6) * mm, v(-4.95, -11.52) * mm, v(-5.02, -11.5) * mm, v(-5.02, -11.56) * mm]});
            skFitSpline(sketch, "E260", {"points": [v(-5.02, -11.56) * mm, v(-5.02, -11.62) * mm, v(-5.21, -11.6) * mm, v(-5.45, -11.51) * mm]});
            skFitSpline(sketch, "E261", {"points": [v(-5.45, -11.51) * mm, v(-5.83, -11.37) * mm, v(-5.91, -11.43) * mm, v(-6.43, -12.3) * mm]});
            skFitSpline(sketch, "E262", {"points": [v(-6.43, -12.3) * mm, v(-7.66, -14.35) * mm, v(-8.1, -15) * mm, v(-8.9, -15.9) * mm]});
            skFitSpline(sketch, "E263", {"points": [v(-8.9, -15.9) * mm, v(-9.63, -16.73) * mm, v(-10.48, -17.39) * mm, v(-10.77, -17.33) * mm]});
            skFitSpline(sketch, "E264", {"points": [v(-10.77, -17.33) * mm, v(-10.82, -17.32) * mm, v(-11.09, -17.37) * mm, v(-11.37, -17.43) * mm]});
            skFitSpline(sketch, "E265", {"points": [v(-11.37, -17.43) * mm, v(-11.79, -17.52) * mm, v(-12.15, -17.95) * mm, v(-13.44, -19.89) * mm]});
            skFitSpline(sketch, "E266", {"points": [v(-13.44, -19.89) * mm, v(-16.05, -23.81) * mm, v(-17.13, -26.55) * mm, v(-17.33, -29.73) * mm]});
            skFitSpline(sketch, "E267", {"points": [v(-16.23, -31.1) * mm, v(-13.9, -31.2) * mm, v(-14, -31.24) * mm, v(-12.68, -29.84) * mm]});
            skFitSpline(sketch, "E268", {"points": [v(10.13, -25.33) * mm, v(11.96, -23.13) * mm, v(13.5, -21.5) * mm, v(13.85, -21.4) * mm]});
            skFitSpline(sketch, "E269", {"points": [v(13.85, -21.4) * mm, v(14.11, -21.34) * mm, v(14.5, -21.62) * mm, v(15.43, -22.57) * mm]});
            skFitSpline(sketch, "E270", {"points": [v(15.43, -22.57) * mm, v(16.63, -23.78) * mm, v(20.49, -26.5) * mm, v(21.94, -27.16) * mm]});
            skFitSpline(sketch, "E271", {"points": [v(23.83, -26.21) * mm, v(24.52, -25.53) * mm, v(25.41, -24.49) * mm, v(25.8, -23.89) * mm]});
            skFitSpline(sketch, "E272", {"points": [v(25.8, -23.89) * mm, v(26.8, -22.4) * mm, v(27.58, -19.93) * mm, v(27.7, -17.94) * mm]});
            skFitSpline(sketch, "E273", {"points": [v(27.08, -17.43) * mm, v(25.98, -19.07) * mm, v(24.59, -20.46) * mm, v(24.2, -20.32) * mm]});
            skFitSpline(sketch, "E274", {"points": [v(24.2, -20.32) * mm, v(23.4, -20.02) * mm, v(23.44, -19.37) * mm, v(24.32, -18.57) * mm]});
            skFitSpline(sketch, "E275", {"points": [v(24.32, -18.57) * mm, v(26.2, -16.9) * mm, v(28.34, -12.27) * mm, v(28.54, -9.5) * mm]});
            skFitSpline(sketch, "E276", {"points": [v(28.54, -9.5) * mm, v(28.6, -8.81) * mm, v(28.59, -8.25) * mm, v(28.53, -8.25) * mm]});
            skFitSpline(sketch, "E277", {"points": [v(28.53, -8.25) * mm, v(28.47, -8.25) * mm, v(27.98, -8.48) * mm, v(27.44, -8.76) * mm]});
            skFitSpline(sketch, "E278", {"points": [v(27.44, -8.76) * mm, v(25.7, -9.64) * mm, v(24.76, -10.02) * mm, v(21.65, -11.08) * mm]});
            skFitSpline(sketch, "E279", {"points": [v(21.65, -11.08) * mm, v(20.99, -11.3) * mm, v(20.25, -11.53) * mm, v(20.02, -11.57) * mm]});
            skFitSpline(sketch, "E280", {"points": [v(20.02, -11.57) * mm, v(19.78, -11.62) * mm, v(19.2, -11.74) * mm, v(18.73, -11.84) * mm]});
            skFitSpline(sketch, "E281", {"points": [v(18.73, -11.84) * mm, v(17.26, -12.15) * mm, v(16.89, -12.2) * mm, v(15.3, -12.3) * mm]});
            skFitSpline(sketch, "E282", {"points": [v(15.3, -12.3) * mm, v(12.58, -12.45) * mm, v(12.24, -12.52) * mm, v(10.93, -13.17) * mm]});
            skFitSpline(sketch, "E283", {"points": [v(10.93, -13.17) * mm, v(10, -13.63) * mm, v(9.31, -14.14) * mm, v(8.43, -15.05) * mm]});
            skFitSpline(sketch, "E284", {"points": [v(8.43, -15.05) * mm, v(6.45, -17.07) * mm, v(5.44, -19.39) * mm, v(5.44, -21.88) * mm]});
            skFitSpline(sketch, "E285", {"points": [v(5.44, -21.88) * mm, v(5.44, -23.96) * mm, v(6.02, -25.51) * mm, v(7.35, -27.02) * mm]});
            skFitSpline(sketch, "E286", {"points": [v(8.6, -27.2) * mm, v(8.9, -26.85) * mm, v(9.58, -26) * mm, v(10.13, -25.33) * mm]});
            skFitSpline(sketch, "E287", {"points": [v(-13.63, -16.05) * mm, v(-14.66, -14.25) * mm, v(-15.02, -12.98) * mm, v(-15.04, -10.97) * mm]});
            skFitSpline(sketch, "E288", {"points": [v(-15.04, -10.97) * mm, v(-15.05, -10.15) * mm, v(-15.1, -9.43) * mm, v(-15.16, -9.37) * mm]});
            skFitSpline(sketch, "E289", {"points": [v(-15.16, -9.37) * mm, v(-15.22, -9.31) * mm, v(-15.48, -9.23) * mm, v(-15.73, -9.18) * mm]});
            skFitSpline(sketch, "E290", {"points": [v(-15.73, -9.18) * mm, v(-16.87, -8.98) * mm, v(-19.8, -7.6) * mm, v(-20.55, -6.93) * mm]});
            skFitSpline(sketch, "E291", {"points": [v(-20.55, -6.93) * mm, v(-20.74, -6.76) * mm, v(-21.5, -6.1) * mm, v(-22.26, -5.48) * mm]});
            skFitSpline(sketch, "E292", {"points": [v(-22.26, -5.48) * mm, v(-23.71, -4.28) * mm, v(-24.41, -3.56) * mm, v(-24.74, -2.94) * mm]});
            skFitSpline(sketch, "E293", {"points": [v(-24.74, -2.94) * mm, v(-24.86, -2.73) * mm, v(-24.98, -2.6) * mm, v(-25.01, -2.63) * mm]});
            skFitSpline(sketch, "E294", {"points": [v(-25.01, -2.63) * mm, v(-25.18, -2.8) * mm, v(-25.32, -4.03) * mm, v(-25.32, -5.34) * mm]});
            skFitSpline(sketch, "E295", {"points": [v(-25.32, -5.34) * mm, v(-25.3, -7.02) * mm, v(-24.99, -7.98) * mm, v(-24.33, -8.28) * mm]});
            skFitSpline(sketch, "E296", {"points": [v(-24.33, -8.28) * mm, v(-24.05, -8.4) * mm, v(-23.9, -8.62) * mm, v(-23.9, -8.85) * mm]});
            skFitSpline(sketch, "E297", {"points": [v(-23.9, -8.85) * mm, v(-23.9, -9.52) * mm, v(-22.62, -11.04) * mm, v(-20.87, -12.48) * mm]});
            skFitSpline(sketch, "E298", {"points": [v(-20.87, -12.48) * mm, v(-20.46, -12.82) * mm, v(-20.12, -13.24) * mm, v(-20.12, -13.4) * mm]});
            skFitSpline(sketch, "E299", {"points": [v(-20.12, -13.4) * mm, v(-20.12, -13.8) * mm, v(-20.56, -14.26) * mm, v(-20.95, -14.26) * mm]});
            skFitSpline(sketch, "E300", {"points": [v(-20.95, -14.26) * mm, v(-21.28, -14.26) * mm, v(-23.23, -12.6) * mm, v(-23.93, -11.72) * mm]});
            skFitSpline(sketch, "E301", {"points": [v(-23.93, -11.72) * mm, v(-24.19, -11.4) * mm, v(-24.41, -11.23) * mm, v(-24.42, -11.36) * mm]});
            skFitSpline(sketch, "E302", {"points": [v(-24.42, -11.36) * mm, v(-24.69, -14.77) * mm, v(-23.47, -17.67) * mm, v(-20.86, -19.82) * mm]});
            skFitSpline(sketch, "E303", {"points": [v(-20.86, -19.82) * mm, v(-19.81, -20.69) * mm, v(-18.44, -21.47) * mm, v(-17.2, -21.9) * mm]});
            skFitSpline(sketch, "E304", {"points": [v(-15.58, -20.48) * mm, v(-15, -19.58) * mm, v(-14.23, -18.4) * mm, v(-13.84, -17.87) * mm]});
            skFitSpline(sketch, "E305", {"points": [v(1.84, -19.55) * mm, v(2.17, -19.35) * mm, v(2.61, -18.98) * mm, v(2.83, -18.73) * mm]});
            skFitSpline(sketch, "E306", {"points": [v(2.83, -18.73) * mm, v(3.4, -18.09) * mm, v(4.77, -15.14) * mm, v(5, -14.08) * mm]});
            skFitSpline(sketch, "E307", {"points": [v(5, -14.08) * mm, v(5.04, -13.94) * mm, v(5.22, -13.2) * mm, v(5.4, -12.45) * mm]});
            skFitSpline(sketch, "E308", {"points": [v(5.4, -12.45) * mm, v(5.6, -11.7) * mm, v(5.8, -10.77) * mm, v(5.84, -10.4) * mm]});
            skFitSpline(sketch, "E309", {"points": [v(5.84, -10.4) * mm, v(5.9, -10.02) * mm, v(5.98, -9.6) * mm, v(6.03, -9.45) * mm]});
            skFitSpline(sketch, "E310", {"points": [v(6.03, -9.45) * mm, v(6.12, -9.22) * mm, v(6.17, -8.72) * mm, v(6.37, -6.1) * mm]});
            skFitSpline(sketch, "E311", {"points": [v(6.37, -6.1) * mm, v(6.57, -3.6) * mm, v(6.45, -2.69) * mm, v(5.8, -1.62) * mm]});
            skFitSpline(sketch, "E312", {"points": [v(5.8, -1.62) * mm, v(5.08, -0.45) * mm, v(4.12, -0.22) * mm, v(2.46, -0.8) * mm]});
            skFitSpline(sketch, "E313", {"points": [v(2.46, -0.8) * mm, v(1.17, -1.25) * mm, v(0.67, -1.6) * mm, v(-0.64, -2.88) * mm]});
            skFitSpline(sketch, "E314", {"points": [v(-0.64, -2.88) * mm, v(-2.78, -5) * mm, v(-3.34, -6.58) * mm, v(-3.35, -10.48) * mm]});
            skFitSpline(sketch, "E315", {"points": [v(-3.35, -10.48) * mm, v(-3.35, -13.7) * mm, v(-2.42, -17.22) * mm, v(-1.11, -18.95) * mm]});
            skFitSpline(sketch, "E316", {"points": [v(-1.11, -18.95) * mm, v(-0.35, -19.95) * mm, v(0.8, -20.18) * mm, v(1.84, -19.55) * mm]});
            skFitSpline(sketch, "E317", {"points": [v(-10.04, -14.94) * mm, v(-9.58, -14.51) * mm, v(-8.08, -12.28) * mm, v(-7.49, -11.15) * mm]});
            skFitSpline(sketch, "E318", {"points": [v(-7.49, -11.15) * mm, v(-7.1, -10.4) * mm, v(-7.09, -10.34) * mm, v(-7.34, -9.63) * mm]});
            skFitSpline(sketch, "E319", {"points": [v(-7.34, -9.63) * mm, v(-7.67, -8.67) * mm, v(-7.46, -5.55) * mm, v(-7, -4.65) * mm]});
            skFitSpline(sketch, "E320", {"points": [v(-8.1, -3.28) * mm, v(-8.85, -2.8) * mm, v(-9.73, -2.13) * mm, v(-10.05, -1.82) * mm]});
            skFitSpline(sketch, "E321", {"points": [v(-10.05, -1.82) * mm, v(-10.6, -1.28) * mm, v(-10.67, -1.26) * mm, v(-10.9, -1.53) * mm]});
            skFitSpline(sketch, "E322", {"points": [v(-10.9, -1.53) * mm, v(-11.4, -2.14) * mm, v(-11.9, -3.17) * mm, v(-12.47, -4.87) * mm]});
            skFitSpline(sketch, "E323", {"points": [v(-12.47, -4.87) * mm, v(-13.22, -7.09) * mm, v(-13.54, -8.82) * mm, v(-13.59, -10.87) * mm]});
            skFitSpline(sketch, "E324", {"points": [v(-13.59, -10.87) * mm, v(-13.62, -12.44) * mm, v(-13.6, -12.54) * mm, v(-12.92, -13.96) * mm]});
            skFitSpline(sketch, "E325", {"points": [v(-12.92, -13.96) * mm, v(-11.98, -15.94) * mm, v(-11.33, -16.16) * mm, v(-10.04, -14.94) * mm]});
            skFitSpline(sketch, "E326", {"points": [v(8.48, -12.99) * mm, v(9.07, -12.54) * mm, v(9.56, -12.12) * mm, v(9.56, -12.04) * mm]});
            skFitSpline(sketch, "E327", {"points": [v(9.56, -12.04) * mm, v(9.56, -11.83) * mm, v(8.27, -9.9) * mm, v(7.95, -9.64) * mm]});
            skFitSpline(sketch, "E328", {"points": [v(7.95, -9.64) * mm, v(7.6, -9.35) * mm, v(7.55, -9.39) * mm, v(7.45, -10.14) * mm]});
            skFitSpline(sketch, "E329", {"points": [v(7.45, -10.14) * mm, v(7.38, -10.64) * mm, v(6.9, -12.63) * mm, v(6.36, -14.6) * mm]});
            skFitSpline(sketch, "E330", {"points": [v(6.36, -14.6) * mm, v(6.25, -15) * mm, v(6.3, -14.98) * mm, v(6.83, -14.41) * mm]});
            skFitSpline(sketch, "E331", {"points": [v(6.83, -14.41) * mm, v(7.15, -14.08) * mm, v(7.9, -13.44) * mm, v(8.48, -12.99) * mm]});
            skFitSpline(sketch, "E332", {"points": [v(-4.82, -9.5) * mm, v(-4.86, -9.18) * mm, v(-4.58, -7.33) * mm, v(-4.25, -5.76) * mm]});
            skFitSpline(sketch, "E333", {"points": [v(-4.25, -5.76) * mm, v(-4.15, -5.3) * mm, v(-4.2, -5.2) * mm, v(-4.59, -5.03) * mm]});
            skFitSpline(sketch, "E334", {"points": [v(-4.59, -5.03) * mm, v(-5.33, -4.7) * mm, v(-5.5, -4.78) * mm, v(-5.79, -5.66) * mm]});
            skFitSpline(sketch, "E335", {"points": [v(-5.79, -5.66) * mm, v(-6.1, -6.57) * mm, v(-6.16, -7.7) * mm, v(-5.97, -8.6) * mm]});
            skFitSpline(sketch, "E336", {"points": [v(-5.97, -8.6) * mm, v(-5.75, -9.62) * mm, v(-4.68, -10.45) * mm, v(-4.82, -9.5) * mm]});
            skFitSpline(sketch, "E337", {"points": [v(10.44, -4.22) * mm, v(11.04, -4.07) * mm, v(12.22, -3.61) * mm, v(13.07, -3.2) * mm]});
            skFitSpline(sketch, "E338", {"points": [v(13.07, -3.2) * mm, v(13.92, -2.8) * mm, v(15.12, -2.23) * mm, v(15.75, -1.93) * mm]});
            skFitSpline(sketch, "E339", {"points": [v(15.75, -1.93) * mm, v(18.02, -0.86) * mm, v(22.95, 3.35) * mm, v(25.2, 6.13) * mm]});
            skFitSpline(sketch, "E340", {"points": [v(25.2, 6.13) * mm, v(27.13, 8.54) * mm, v(28.75, 11.32) * mm, v(29.2, 13.04) * mm]});
            skFitSpline(sketch, "E341", {"points": [v(28.41, 15.23) * mm, v(27.85, 15.95) * mm, v(27.33, 16.6) * mm, v(27.26, 16.7) * mm]});
            skFitSpline(sketch, "E342", {"points": [v(27.26, 16.7) * mm, v(27.19, 16.8) * mm, v(26.89, 17.18) * mm, v(26.58, 17.55) * mm]});
            skFitSpline(sketch, "E343", {"points": [v(26.58, 17.55) * mm, v(26.28, 17.92) * mm, v(26.08, 18.29) * mm, v(26.13, 18.37) * mm]});
            skFitSpline(sketch, "E344", {"points": [v(26.13, 18.37) * mm, v(26.18, 18.45) * mm, v(26.14, 18.5) * mm, v(26.05, 18.47) * mm]});
            skFitSpline(sketch, "E345", {"points": [v(26.05, 18.47) * mm, v(25.96, 18.44) * mm, v(25.16, 19.27) * mm, v(24.27, 20.3) * mm]});
            skFitSpline(sketch, "E346", {"points": [v(24.27, 20.3) * mm, v(22.24, 22.66) * mm, v(21.28, 23.65) * mm, v(21.05, 23.65) * mm]});
            skFitSpline(sketch, "E347", {"points": [v(21.05, 23.65) * mm, v(20.62, 23.65) * mm, v(15.52, 22.12) * mm, v(14.36, 21.64) * mm]});
            skFitSpline(sketch, "E348", {"points": [v(14.36, 21.64) * mm, v(14.22, 21.58) * mm, v(14.04, 21.52) * mm, v(13.97, 21.5) * mm]});
            skFitSpline(sketch, "E349", {"points": [v(13.97, 21.5) * mm, v(13.9, 21.48) * mm, v(13.8, 21.44) * mm, v(13.76, 21.42) * mm]});
            skFitSpline(sketch, "E350", {"points": [v(13.76, 21.42) * mm, v(13.71, 21.4) * mm, v(13.61, 21.37) * mm, v(13.54, 21.35) * mm]});
            skFitSpline(sketch, "E351", {"points": [v(13.54, 21.35) * mm, v(13.43, 21.33) * mm, v(11.16, 20.54) * mm, v(10.41, 20.26) * mm]});
            skFitSpline(sketch, "E352", {"points": [v(10.41, 20.26) * mm, v(10.27, 20.21) * mm, v(10.08, 20.15) * mm, v(9.98, 20.12) * mm]});
            skFitSpline(sketch, "E353", {"points": [v(9.98, 20.12) * mm, v(9.89, 20.1) * mm, v(8.98, 19.72) * mm, v(7.95, 19.3) * mm]});
            skFitSpline(sketch, "E354", {"points": [v(7.95, 19.3) * mm, v(6.93, 18.86) * mm, v(5.95, 18.5) * mm, v(5.78, 18.5) * mm]});
            skFitSpline(sketch, "E355", {"points": [v(5.78, 18.5) * mm, v(5.6, 18.5) * mm, v(5.35, 18.39) * mm, v(5.2, 18.25) * mm]});
            skFitSpline(sketch, "E356", {"points": [v(5.2, 18.25) * mm, v(4.58, 17.62) * mm, v(4.02, 18.08) * mm, v(3.96, 19.28) * mm]});
            skFitSpline(sketch, "E357", {"points": [v(3.96, 19.28) * mm, v(3.94, 19.76) * mm, v(3.85, 20.22) * mm, v(3.65, 20.88) * mm]});
            skFitSpline(sketch, "E358", {"points": [v(3.65, 20.88) * mm, v(3.6, 21.03) * mm, v(3.53, 21.4) * mm, v(3.48, 21.68) * mm]});
            skFitSpline(sketch, "E359", {"points": [v(3.48, 21.68) * mm, v(2.72, 26.4) * mm, v(2.52, 27.3) * mm, v(1.96, 28.65) * mm]});
            skFitSpline(sketch, "E360", {"points": [v(0.99, 28.8) * mm, v(0.56, 28.63) * mm, v(-0.37, 28.37) * mm, v(-1.08, 28.2) * mm]});
            skFitSpline(sketch, "E361", {"points": [v(-1.08, 28.2) * mm, v(-2.41, 27.9) * mm, v(-8.03, 25.77) * mm, v(-9.01, 25.2) * mm]});
            skFitSpline(sketch, "E362", {"points": [v(-9.01, 25.2) * mm, v(-9.94, 24.65) * mm, v(-10.51, 24.9) * mm, v(-10.52, 25.85) * mm]});
            skFitSpline(sketch, "E363", {"points": [v(-10.52, 25.85) * mm, v(-10.52, 26.2) * mm, v(-10.6, 26.79) * mm, v(-10.7, 27.17) * mm]});
            skFitSpline(sketch, "E364", {"points": [v(-10.7, 27.17) * mm, v(-10.79, 27.54) * mm, v(-10.9, 27.97) * mm, v(-10.93, 28.11) * mm]});
            skFitSpline(sketch, "E365", {"points": [v(-10.93, 28.11) * mm, v(-10.96, 28.26) * mm, v(-11.25, 29.03) * mm, v(-11.56, 29.83) * mm]});
            skFitSpline(sketch, "E366", {"points": [v(-11.56, 29.83) * mm, v(-11.87, 30.63) * mm, v(-12.11, 31.34) * mm, v(-12.1, 31.41) * mm]});
            skFitSpline(sketch, "E367", {"points": [v(-12.1, 31.41) * mm, v(-11.9, 32.09) * mm, v(-13.38, 30.57) * mm, v(-14.89, 28.54) * mm]});
            skFitSpline(sketch, "E368", {"points": [v(-15.46, 26.94) * mm, v(-14.4, 26.84) * mm, v(-13.5, 25.3) * mm, v(-13.33, 23.3) * mm]});
            skFitSpline(sketch, "E369", {"points": [v(-13.33, 23.3) * mm, v(-13.29, 22.8) * mm, v(-13.2, 22.34) * mm, v(-13.16, 22.25) * mm]});
            skFitSpline(sketch, "E370", {"points": [v(-13.16, 22.25) * mm, v(-13, 22) * mm, v(-13.27, 21.08) * mm, v(-13.5, 21.08) * mm]});
            skFitSpline(sketch, "E371", {"points": [v(-13.5, 21.08) * mm, v(-13.78, 21.08) * mm, v(-13.94, 21.45) * mm, v(-13.94, 22.06) * mm]});
            skFitSpline(sketch, "E372", {"points": [v(-13.94, 22.06) * mm, v(-13.94, 22.3) * mm, v(-14.04, 22.63) * mm, v(-14.17, 22.78) * mm]});
            skFitSpline(sketch, "E373", {"points": [v(-14.17, 22.78) * mm, v(-14.3, 22.93) * mm, v(-14.5, 23.37) * mm, v(-14.6, 23.77) * mm]});
            skFitSpline(sketch, "E374", {"points": [v(-14.6, 23.77) * mm, v(-14.87, 24.7) * mm, v(-15.57, 25.3) * mm, v(-16.04, 24.98) * mm]});
            skFitSpline(sketch, "E375", {"points": [v(-16.04, 24.98) * mm, v(-16.22, 24.86) * mm, v(-16.37, 24.69) * mm, v(-16.37, 24.6) * mm]});
            skFitSpline(sketch, "E376", {"points": [v(-16.37, 24.6) * mm, v(-16.37, 24.34) * mm, v(-16.88, 23.82) * mm, v(-17.14, 23.82) * mm]});
            skFitSpline(sketch, "E377", {"points": [v(-17.14, 23.82) * mm, v(-17.33, 23.82) * mm, v(-17.79, 23.2) * mm, v(-17.77, 22.96) * mm]});
            skFitSpline(sketch, "E378", {"points": [v(-17.77, 22.96) * mm, v(-17.76, 22.92) * mm, v(-17.79, 22.8) * mm, v(-17.82, 22.7) * mm]});
            skFitSpline(sketch, "E379", {"points": [v(-17.82, 22.7) * mm, v(-18.38, 21.22) * mm, v(-18.79, 16.56) * mm, v(-18.42, 15.96) * mm]});
            skFitSpline(sketch, "E380", {"points": [v(-18.42, 15.96) * mm, v(-18.32, 15.8) * mm, v(-17.89, 15.8) * mm, v(-16.53, 15.95) * mm]});
            skFitSpline(sketch, "E381", {"points": [v(-16.53, 15.95) * mm, v(-14.87, 16.13) * mm, v(-14.73, 16.12) * mm, v(-14.3, 15.8) * mm]});
            skFitSpline(sketch, "E382", {"points": [v(-14.3, 15.8) * mm, v(-14.06, 15.62) * mm, v(-13.78, 15.32) * mm, v(-13.69, 15.14) * mm]});
            skFitSpline(sketch, "E383", {"points": [v(-13.69, 15.14) * mm, v(-12.24, 12.37) * mm, v(-9.8, 10.3) * mm, v(-7.05, 9.5) * mm]});
            skFitSpline(sketch, "E384", {"points": [v(-7.05, 9.5) * mm, v(-5.98, 9.2) * mm, v(-5.77, 9.02) * mm, v(-5.54, 8.23) * mm]});
            skFitSpline(sketch, "E385", {"points": [v(-5.54, 8.23) * mm, v(-5.38, 7.67) * mm, v(-5.61, 7.28) * mm, v(-7.29, 5.28) * mm]});
            skFitSpline(sketch, "E386", {"points": [v(-7.29, 5.28) * mm, v(-8.82, 3.46) * mm, v(-10.34, 1.28) * mm, v(-10.34, 0.92) * mm]});
            skFitSpline(sketch, "E387", {"points": [v(-10.34, 0.92) * mm, v(-10.33, 0.65) * mm, v(-9.13, -0.57) * mm, v(-8.1, -1.34) * mm]});
            skFitSpline(sketch, "E388", {"points": [v(-8.1, -1.34) * mm, v(-7.13, -2.07) * mm, v(-5.67, -2.85) * mm, v(-4.31, -3.35) * mm]});
            skFitSpline(sketch, "E389", {"points": [v(-1.91, -2.03) * mm, v(-0.18, -0.28) * mm, v(1.06, 0.47) * mm, v(2.84, 0.85) * mm]});
            skFitSpline(sketch, "E390", {"points": [v(2.84, 0.85) * mm, v(5.69, 1.46) * mm, v(7.46, 0.11) * mm, v(7.76, -2.86) * mm]});
            skFitSpline(sketch, "E391", {"points": [v(7.76, -2.86) * mm, v(7.94, -4.67) * mm, v(7.93, -4.64) * mm, v(8.68, -4.57) * mm]});
            skFitSpline(sketch, "E392", {"points": [v(8.68, -4.57) * mm, v(9.05, -4.53) * mm, v(9.84, -4.37) * mm, v(10.44, -4.22) * mm]});
            skFitSpline(sketch, "E393", {"points": [v(4.08, 7.17) * mm, v(3.91, 7.28) * mm, v(3.83, 7.74) * mm, v(3.81, 8.77) * mm]});
            skFitSpline(sketch, "E394", {"points": [v(3.81, 8.77) * mm, v(3.8, 9.8) * mm, v(3.7, 10.33) * mm, v(3.5, 10.62) * mm]});
            skFitSpline(sketch, "E395", {"points": [v(3.5, 10.62) * mm, v(3.34, 10.85) * mm, v(3.2, 11.23) * mm, v(3.2, 11.47) * mm]});
            skFitSpline(sketch, "E396", {"points": [v(3.2, 11.47) * mm, v(3.2, 12.42) * mm, v(2.1, 13.59) * mm, v(1.63, 13.14) * mm]});
            skFitSpline(sketch, "E397", {"points": [v(1.63, 13.14) * mm, v(0.97, 12.54) * mm, v(-1.1, 11.74) * mm, v(-1.6, 11.9) * mm]});
            skFitSpline(sketch, "E398", {"points": [v(-1.6, 11.9) * mm, v(-1.87, 12) * mm, v(-1.94, 12.14) * mm, v(-1.9, 12.53) * mm]});
            skFitSpline(sketch, "E399", {"points": [v(-1.9, 12.53) * mm, v(-1.86, 12.97) * mm, v(-1.72, 13.09) * mm, v(-0.83, 13.45) * mm]});
            skFitSpline(sketch, "E400", {"points": [v(-0.83, 13.45) * mm, v(-0.27, 13.68) * mm, v(0.52, 14.1) * mm, v(0.93, 14.4) * mm]});
            skFitSpline(sketch, "E401", {"points": [v(0.93, 14.4) * mm, v(1.57, 14.86) * mm, v(1.78, 14.92) * mm, v(2.4, 14.83) * mm]});
            skFitSpline(sketch, "E402", {"points": [v(2.4, 14.83) * mm, v(3.25, 14.71) * mm, v(3.69, 14.26) * mm, v(4.44, 12.72) * mm]});
            skFitSpline(sketch, "E403", {"points": [v(4.44, 12.72) * mm, v(4.92, 11.71) * mm, v(5, 11.63) * mm, v(5.67, 11.52) * mm]});
            skFitSpline(sketch, "E404", {"points": [v(5.67, 11.52) * mm, v(6.64, 11.35) * mm, v(7.71, 11.42) * mm, v(8.74, 11.73) * mm]});
            skFitSpline(sketch, "E405", {"points": [v(8.74, 11.73) * mm, v(9.7, 12) * mm, v(12.58, 13.5) * mm, v(13.45, 14.15) * mm]});
            skFitSpline(sketch, "E406", {"points": [v(13.45, 14.15) * mm, v(13.75, 14.37) * mm, v(14.12, 14.56) * mm, v(14.27, 14.56) * mm]});
            skFitSpline(sketch, "E407", {"points": [v(14.27, 14.56) * mm, v(14.5, 14.56) * mm, v(14.45, 14.36) * mm, v(13.98, 13.51) * mm]});
            skFitSpline(sketch, "E408", {"points": [v(13.98, 13.51) * mm, v(13.43, 12.5) * mm, v(13.35, 12.44) * mm, v(11.7, 11.6) * mm]});
            skFitSpline(sketch, "E409", {"points": [v(11.7, 11.6) * mm, v(9.54, 10.52) * mm, v(8.44, 10.14) * mm, v(7.03, 10) * mm]});
            skFitSpline(sketch, "E410", {"points": [v(6.58, 9.65) * mm, v(6.94, 9.52) * mm, v(7.59, 9.37) * mm, v(8.01, 9.31) * mm]});
            skFitSpline(sketch, "E411", {"points": [v(8.01, 9.31) * mm, v(8.44, 9.25) * mm, v(8.83, 9.18) * mm, v(8.88, 9.15) * mm]});
            skFitSpline(sketch, "E412", {"points": [v(8.88, 9.15) * mm, v(9.17, 8.98) * mm, v(11.43, 9.47) * mm, v(12.07, 9.85) * mm]});
            skFitSpline(sketch, "E413", {"points": [v(12.07, 9.85) * mm, v(13.1, 10.45) * mm, v(13.29, 10.37) * mm, v(12.62, 9.62) * mm]});
            skFitSpline(sketch, "E414", {"points": [v(12.62, 9.62) * mm, v(12.3, 9.27) * mm, v(11.85, 8.74) * mm, v(11.62, 8.44) * mm]});
            skFitSpline(sketch, "E415", {"points": [v(9.22, 7.89) * mm, v(8, 7.87) * mm, v(6.9, 7.96) * mm, v(6.34, 8.11) * mm]});
            skFitSpline(sketch, "E416", {"points": [v(6.34, 8.11) * mm, v(5.84, 8.24) * mm, v(5.43, 8.34) * mm, v(5.43, 8.33) * mm]});
            skFitSpline(sketch, "E417", {"points": [v(5.43, 8.33) * mm, v(5.42, 8.31) * mm, v(5.38, 8.11) * mm, v(5.34, 7.88) * mm]});
            skFitSpline(sketch, "E418", {"points": [v(5.34, 7.88) * mm, v(5.2, 7.1) * mm, v(4.67, 6.8) * mm, v(4.08, 7.17) * mm]});
            skFitSpline(sketch, "E419", {"points": [v(-13.4, -0.4) * mm, v(-13.16, -0.15) * mm, v(-12.79, 0.38) * mm, v(-12.57, 0.75) * mm]});
            skFitSpline(sketch, "E420", {"points": [v(-12.57, 0.75) * mm, v(-12.35, 1.13) * mm, v(-11.7, 2.02) * mm, v(-11.15, 2.73) * mm]});
            skFitSpline(sketch, "E421", {"points": [v(-11.15, 2.73) * mm, v(-8.69, 5.87) * mm, v(-7.27, 7.83) * mm, v(-7.38, 7.94) * mm]});
            skFitSpline(sketch, "E422", {"points": [v(-7.38, 7.94) * mm, v(-7.6, 8.16) * mm, v(-7.9, 8.03) * mm, v(-7.84, 7.74) * mm]});
            skFitSpline(sketch, "E423", {"points": [v(-7.84, 7.74) * mm, v(-7.75, 7.35) * mm, v(-7.98, 7.07) * mm, v(-9.2, 6.12) * mm]});
            skFitSpline(sketch, "E424", {"points": [v(-9.2, 6.12) * mm, v(-9.76, 5.68) * mm, v(-10.54, 4.86) * mm, v(-10.94, 4.29) * mm]});
            skFitSpline(sketch, "E425", {"points": [v(-10.94, 4.29) * mm, v(-11.34, 3.72) * mm, v(-11.73, 3.3) * mm, v(-11.8, 3.37) * mm]});
            skFitSpline(sketch, "E426", {"points": [v(-11.8, 3.37) * mm, v(-11.88, 3.44) * mm, v(-11.89, 3.41) * mm, v(-11.83, 3.3) * mm]});
            skFitSpline(sketch, "E427", {"points": [v(-11.83, 3.3) * mm, v(-11.77, 3.2) * mm, v(-11.94, 2.81) * mm, v(-12.2, 2.45) * mm]});
            skFitSpline(sketch, "E428", {"points": [v(-12.2, 2.45) * mm, v(-13.4, 0.83) * mm, v(-14.15, 0.66) * mm, v(-14.76, 1.86) * mm]});
            skFitSpline(sketch, "E429", {"points": [v(-14.76, 1.86) * mm, v(-15.17, 2.69) * mm, v(-15.23, 2.64) * mm, v(-14.98, 1.7) * mm]});
            skFitSpline(sketch, "E430", {"points": [v(-14.98, 1.7) * mm, v(-14.9, 1.37) * mm, v(-14.8, 0.82) * mm, v(-14.75, 0.48) * mm]});
            skFitSpline(sketch, "E431", {"points": [v(-14.75, 0.48) * mm, v(-14.66, -0.27) * mm, v(-14.35, -0.88) * mm, v(-14.05, -0.88) * mm]});
            skFitSpline(sketch, "E432", {"points": [v(-14.05, -0.88) * mm, v(-13.93, -0.88) * mm, v(-13.64, -0.66) * mm, v(-13.4, -0.4) * mm]});
            skFitSpline(sketch, "E433", {"points": [v(-11.54, 6.2) * mm, v(-11.54, 6.27) * mm, v(-12.13, 6.38) * mm, v(-13.81, 6.6) * mm]});
            skFitSpline(sketch, "E434", {"points": [v(-13.81, 6.6) * mm, v(-14.26, 6.66) * mm, v(-14.29, 6.63) * mm, v(-14.28, 5.94) * mm]});
            skFitSpline(sketch, "E435", {"points": [v(-14.28, 5.94) * mm, v(-14.28, 5.24) * mm, v(-13.93, 3.64) * mm, v(-13.7, 3.26) * mm]});
            skFitSpline(sketch, "E436", {"points": [v(-13.7, 3.26) * mm, v(-13.6, 3.1) * mm, v(-11.54, 5.93) * mm, v(-11.54, 6.2) * mm]});
            skFitSpline(sketch, "E437", {"points": [v(-9.55, 8.72) * mm, v(-10, 8.93) * mm, v(-10.45, 9.2) * mm, v(-10.56, 9.3) * mm]});
            skFitSpline(sketch, "E438", {"points": [v(-10.56, 9.3) * mm, v(-10.68, 9.42) * mm, v(-11.12, 9.77) * mm, v(-11.54, 10.09) * mm]});
            skFitSpline(sketch, "E439", {"points": [v(-11.54, 10.09) * mm, v(-12.97, 11.17) * mm, v(-13.97, 12.24) * mm, v(-14.47, 13.22) * mm]});
            skFitSpline(sketch, "E440", {"points": [v(-14.47, 13.22) * mm, v(-15.02, 14.31) * mm, v(-15.36, 14.57) * mm, v(-16.1, 14.48) * mm]});
            skFitSpline(sketch, "E441", {"points": [v(-16.1, 14.48) * mm, v(-16.38, 14.45) * mm, v(-17.1, 14.37) * mm, v(-17.72, 14.3) * mm]});
            skFitSpline(sketch, "E442", {"points": [v(-17.72, 14.3) * mm, v(-18.33, 14.24) * mm, v(-19.1, 14.12) * mm, v(-19.43, 14.04) * mm]});
            skFitSpline(sketch, "E443", {"points": [v(-19.43, 14.04) * mm, v(-19.76, 13.96) * mm, v(-20.3, 13.84) * mm, v(-20.63, 13.79) * mm]});
            skFitSpline(sketch, "E444", {"points": [v(-20.63, 13.79) * mm, v(-20.96, 13.73) * mm, v(-21.35, 13.66) * mm, v(-21.49, 13.61) * mm]});
            skFitSpline(sketch, "E445", {"points": [v(-21.49, 13.61) * mm, v(-21.63, 13.57) * mm, v(-22.04, 13.5) * mm, v(-22.4, 13.46) * mm]});
            skFitSpline(sketch, "E446", {"points": [v(-22.4, 13.46) * mm, v(-22.77, 13.42) * mm, v(-23.1, 13.34) * mm, v(-23.15, 13.3) * mm]});
            skFitSpline(sketch, "E447", {"points": [v(-23.15, 13.3) * mm, v(-23.42, 13.03) * mm, v(-20.05, 10.6) * mm, v(-17.88, 9.5) * mm]});
            skFitSpline(sketch, "E448", {"points": [v(-17.88, 9.5) * mm, v(-15.24, 8.16) * mm, v(-11.42, 7.53) * mm, v(-9.5, 8.1) * mm]});
            skFitSpline(sketch, "E449", {"points": [v(34.87, 13.62) * mm, v(34.9, 15.22) * mm, v(35, 17.19) * mm, v(35.07, 18) * mm]});
            skFitSpline(sketch, "E450", {"points": [v(35.07, 18) * mm, v(35.26, 20.03) * mm, v(35.12, 28.3) * mm, v(34.85, 30.94) * mm]});
            skFitSpline(sketch, "E451", {"points": [v(34.85, 30.94) * mm, v(34.72, 32.23) * mm, v(34.49, 34.02) * mm, v(34.23, 35.66) * mm]});
            skFitSpline(sketch, "E452", {"points": [v(34.23, 35.66) * mm, v(34.13, 36.27) * mm, v(34.02, 37) * mm, v(33.99, 37.29) * mm]});
            skFitSpline(sketch, "E453", {"points": [v(33.99, 37.29) * mm, v(33.95, 37.57) * mm, v(33.87, 38.01) * mm, v(33.82, 38.27) * mm]});
            skFitSpline(sketch, "E454", {"points": [v(33.82, 38.27) * mm, v(33.76, 38.53) * mm, v(33.7, 38.8) * mm, v(33.7, 38.87) * mm]});
            skFitSpline(sketch, "E455", {"points": [v(33.7, 38.87) * mm, v(33.7, 38.94) * mm, v(33.63, 39.18) * mm, v(33.55, 39.4) * mm]});
            skFitSpline(sketch, "E456", {"points": [v(33.55, 39.4) * mm, v(33.47, 39.61) * mm, v(33.35, 40.04) * mm, v(33.3, 40.34) * mm]});
            skFitSpline(sketch, "E457", {"points": [v(33.3, 40.34) * mm, v(32.92, 42.51) * mm, v(31.3, 46.86) * mm, v(29.93, 49.38) * mm]});
            skFitSpline(sketch, "E458", {"points": [v(29.93, 49.38) * mm, v(29.54, 50.09) * mm, v(28.96, 51.15) * mm, v(28.64, 51.75) * mm]});
            skFitSpline(sketch, "E459", {"points": [v(28.64, 51.75) * mm, v(27.69, 53.55) * mm, v(27.22, 54.21) * mm, v(26.12, 55.36) * mm]});
            skFitSpline(sketch, "E460", {"points": [v(26.12, 55.36) * mm, v(25, 56.53) * mm, v(23, 58.12) * mm, v(21.72, 58.87) * mm]});
            skFitSpline(sketch, "E461", {"points": [v(21.72, 58.87) * mm, v(21.04, 59.26) * mm, v(18.95, 60.08) * mm, v(18.13, 60.27) * mm]});
            skFitSpline(sketch, "E462", {"points": [v(18.13, 60.27) * mm, v(17.99, 60.3) * mm, v(17.64, 60.42) * mm, v(17.36, 60.53) * mm]});
            skFitSpline(sketch, "E463", {"points": [v(17.36, 60.53) * mm, v(16.42, 60.9) * mm, v(16.18, 60.92) * mm, v(13.5, 60.96) * mm]});
            skFitSpline(sketch, "E464", {"points": [v(13.5, 60.96) * mm, v(11.47, 60.99) * mm, v(10.48, 60.92) * mm, v(9.3, 60.68) * mm]});
            skFitSpline(sketch, "E465", {"points": [v(9.3, 60.68) * mm, v(8.45, 60.5) * mm, v(7.53, 60.32) * mm, v(7.25, 60.27) * mm]});
            skFitSpline(sketch, "E466", {"points": [v(7.25, 60.27) * mm, v(6.98, 60.21) * mm, v(6.7, 60.13) * mm, v(6.61, 60.08) * mm]});
            skFitSpline(sketch, "E467", {"points": [v(6.61, 60.08) * mm, v(6.53, 60.03) * mm, v(6.33, 59.96) * mm, v(6.17, 59.93) * mm]});
            skFitSpline(sketch, "E468", {"points": [v(6.17, 59.93) * mm, v(4.67, 59.62) * mm, v(1.37, 58.01) * mm, v(-1.02, 56.43) * mm]});
            skFitSpline(sketch, "E469", {"points": [v(-1.02, 56.43) * mm, v(-5.55, 53.43) * mm, v(-8.9, 50.47) * mm, v(-15.01, 44.07) * mm]});
            skFitSpline(sketch, "E470", {"points": [v(-15.01, 44.07) * mm, v(-16.79, 42.21) * mm, v(-18.96, 39.22) * mm, v(-20.28, 36.81) * mm]});
            skFitSpline(sketch, "E471", {"points": [v(-20.28, 36.81) * mm, v(-20.9, 35.69) * mm, v(-20.87, 35.67) * mm, v(-19.28, 36.08) * mm]});
            skFitSpline(sketch, "E472", {"points": [v(-19.28, 36.08) * mm, v(-18.75, 36.21) * mm, v(-18.05, 36.37) * mm, v(-17.72, 36.42) * mm]});
            skFitSpline(sketch, "E473", {"points": [v(-17.72, 36.42) * mm, v(-17.39, 36.48) * mm, v(-16.92, 36.55) * mm, v(-16.69, 36.6) * mm]});
            skFitSpline(sketch, "E474", {"points": [v(-16.69, 36.6) * mm, v(-16.45, 36.64) * mm, v(-15.88, 36.72) * mm, v(-15.41, 36.77) * mm]});
            skFitSpline(sketch, "E475", {"points": [v(-15.41, 36.77) * mm, v(-14.95, 36.83) * mm, v(-14.5, 36.92) * mm, v(-14.42, 36.97) * mm]});
            skFitSpline(sketch, "E476", {"points": [v(-14.42, 36.97) * mm, v(-14.34, 37.02) * mm, v(-13.9, 37.1) * mm, v(-13.44, 37.15) * mm]});
            skFitSpline(sketch, "E477", {"points": [v(-13.44, 37.15) * mm, v(-12.7, 37.22) * mm, v(-12.58, 37.19) * mm, v(-12.4, 36.86) * mm]});
            skFitSpline(sketch, "E478", {"points": [v(-12.4, 36.86) * mm, v(-12.3, 36.66) * mm, v(-12.18, 36.36) * mm, v(-12.15, 36.2) * mm]});
            skFitSpline(sketch, "E479", {"points": [v(-12.15, 36.2) * mm, v(-12.11, 36.04) * mm, v(-11.84, 35.22) * mm, v(-11.55, 34.37) * mm]});
            skFitSpline(sketch, "E480", {"points": [v(-11.55, 34.37) * mm, v(-11.25, 33.52) * mm, v(-10.97, 32.71) * mm, v(-10.93, 32.57) * mm]});
            skFitSpline(sketch, "E481", {"points": [v(-10.93, 32.57) * mm, v(-10.9, 32.43) * mm, v(-10.55, 31.4) * mm, v(-10.17, 30.29) * mm]});
            skFitSpline(sketch, "E482", {"points": [v(-10.17, 30.29) * mm, v(-9.8, 29.17) * mm, v(-9.48, 28.1) * mm, v(-9.48, 27.88) * mm]});
            skFitSpline(sketch, "E483", {"points": [v(-9.48, 27.88) * mm, v(-9.48, 27.68) * mm, v(-9.4, 27.4) * mm, v(-9.32, 27.26) * mm]});
            skFitSpline(sketch, "E484", {"points": [v(-9.32, 27.26) * mm, v(-9.13, 26.96) * mm, v(-8.47, 27.14) * mm, v(-4.7, 28.53) * mm]});
            skFitSpline(sketch, "E485", {"points": [v(-4.7, 28.53) * mm, v(-3.26, 29.06) * mm, v(-1.75, 29.57) * mm, v(-1.36, 29.65) * mm]});
            skFitSpline(sketch, "E486", {"points": [v(-1.36, 29.65) * mm, v(-0.1, 29.91) * mm, v(0.03, 29.95) * mm, v(1.02, 30.44) * mm]});
            skFitSpline(sketch, "E487", {"points": [v(1.02, 30.44) * mm, v(2.42, 31.13) * mm, v(2.78, 30.97) * mm, v(3.3, 29.4) * mm]});
            skFitSpline(sketch, "E488", {"points": [v(3.3, 29.4) * mm, v(3.52, 28.74) * mm, v(3.75, 27.9) * mm, v(3.8, 27.54) * mm]});
            skFitSpline(sketch, "E489", {"points": [v(3.8, 27.54) * mm, v(3.85, 27.18) * mm, v(3.92, 26.83) * mm, v(3.97, 26.76) * mm]});
            skFitSpline(sketch, "E490", {"points": [v(3.97, 26.76) * mm, v(4.01, 26.69) * mm, v(4.1, 26.25) * mm, v(4.16, 25.78) * mm]});
            skFitSpline(sketch, "E491", {"points": [v(4.16, 25.78) * mm, v(4.22, 25.32) * mm, v(4.33, 24.63) * mm, v(4.4, 24.25) * mm]});
            skFitSpline(sketch, "E492", {"points": [v(4.4, 24.25) * mm, v(4.46, 23.87) * mm, v(4.5, 23.37) * mm, v(4.5, 23.14) * mm]});
            skFitSpline(sketch, "E493", {"points": [v(4.5, 23.14) * mm, v(4.5, 22.9) * mm, v(4.54, 22.67) * mm, v(4.59, 22.62) * mm]});
            skFitSpline(sketch, "E494", {"points": [v(4.59, 22.62) * mm, v(4.64, 22.57) * mm, v(4.83, 22) * mm, v(5.02, 21.33) * mm]});
            skFitSpline(sketch, "E495", {"points": [v(5.02, 21.33) * mm, v(5.34, 20.2) * mm, v(5.38, 20.13) * mm, v(5.87, 20.12) * mm]});
            skFitSpline(sketch, "E496", {"points": [v(5.87, 20.12) * mm, v(6.4, 20.1) * mm, v(8.27, 20.73) * mm, v(11.01, 21.85) * mm]});
            skFitSpline(sketch, "E497", {"points": [v(11.01, 21.85) * mm, v(11.86, 22.2) * mm, v(12.63, 22.49) * mm, v(12.73, 22.5) * mm]});
            skFitSpline(sketch, "E498", {"points": [v(12.73, 22.5) * mm, v(12.82, 22.53) * mm, v(12.99, 22.6) * mm, v(13.1, 22.67) * mm]});
            skFitSpline(sketch, "E499", {"points": [v(13.1, 22.67) * mm, v(13.2, 22.73) * mm, v(13.59, 22.84) * mm, v(13.95, 22.9) * mm]});
            skFitSpline(sketch, "E500", {"points": [v(13.95, 22.9) * mm, v(14.32, 22.95) * mm, v(14.75, 23.07) * mm, v(14.92, 23.16) * mm]});
            skFitSpline(sketch, "E501", {"points": [v(14.92, 23.16) * mm, v(15.08, 23.25) * mm, v(15.22, 23.29) * mm, v(15.22, 23.25) * mm]});
            skFitSpline(sketch, "E502", {"points": [v(15.22, 23.25) * mm, v(15.22, 23.2) * mm, v(15.93, 23.44) * mm, v(16.8, 23.77) * mm]});
            skFitSpline(sketch, "E503", {"points": [v(16.8, 23.77) * mm, v(17.67, 24.1) * mm, v(18.51, 24.39) * mm, v(18.67, 24.42) * mm]});
            skFitSpline(sketch, "E504", {"points": [v(18.67, 24.42) * mm, v(18.82, 24.45) * mm, v(19.44, 24.68) * mm, v(20.05, 24.92) * mm]});
            skFitSpline(sketch, "E505", {"points": [v(20.05, 24.92) * mm, v(21.36, 25.44) * mm, v(22.04, 25.5) * mm, v(22.2, 25.07) * mm]});
            skFitSpline(sketch, "E506", {"points": [v(22.2, 25.07) * mm, v(22.32, 24.7) * mm, v(23.15, 23.67) * mm, v(24.07, 22.7) * mm]});
            skFitSpline(sketch, "E507", {"points": [v(24.07, 22.7) * mm, v(24.44, 22.32) * mm, v(25.66, 20.85) * mm, v(26.78, 19.44) * mm]});
            skFitSpline(sketch, "E508", {"points": [v(26.78, 19.44) * mm, v(27.91, 18.03) * mm, v(29.1, 16.56) * mm, v(29.44, 16.18) * mm]});
            skFitSpline(sketch, "E509", {"points": [v(29.44, 16.18) * mm, v(29.78, 15.8) * mm, v(30.55, 14.86) * mm, v(31.17, 14.12) * mm]});
            skFitSpline(sketch, "E510", {"points": [v(31.17, 14.12) * mm, v(31.78, 13.37) * mm, v(32.37, 12.66) * mm, v(32.48, 12.54) * mm]});
            skFitSpline(sketch, "E511", {"points": [v(32.48, 12.54) * mm, v(32.6, 12.42) * mm, v(33.1, 11.78) * mm, v(33.6, 11.11) * mm]});
            skFitSpline(sketch, "E512", {"points": [v(33.6, 11.11) * mm, v(34.44, 9.97) * mm, v(34.5, 9.92) * mm, v(34.64, 10.3) * mm]});
            skFitSpline(sketch, "E513", {"points": [v(34.64, 10.3) * mm, v(34.73, 10.52) * mm, v(34.83, 12.01) * mm, v(34.87, 13.62) * mm]});
            skSolve(sketch);
        }
        {
            var Q0;
            Q0=makeQuery(id+"F0.imprint","IMPRINT",FACE,{"disambiguationData":[TD([[makeQuery(id+"F0.imprint","IMPRINT",EDGE,{"derivedFrom":sQuery(id+"F0.wireOp",EDGE,"E449")}),1.0]])]});
            var Q1;
            Q1=makeQuery(id+"F0.imprint","IMPRINT",FACE,{"disambiguationData":[TD([[makeQuery(id+"F0.imprint","IMPRINT",EDGE,{"derivedFrom":sQuery(id+"F0.wireOp",EDGE,"E0")}),-1.0]])]});
            var Q2;
            Q2=makeQuery(id+"F0.imprint","IMPRINT",FACE,{"disambiguationData":[TD([[makeQuery(id+"F0.imprint","IMPRINT",EDGE,{"derivedFrom":sQuery(id+"F0.wireOp",EDGE,"E25")}),1.0]])]});
            var Q3;
            Q3=makeQuery(id+"F0.imprint","IMPRINT",FACE,{"disambiguationData":[TD([[makeQuery(id+"F0.imprint","IMPRINT",EDGE,{"derivedFrom":sQuery(id+"F0.wireOp",EDGE,"E34")}),-1.0]])]});
            var Q4;
            Q4=makeQuery(id+"F0.imprint","IMPRINT",FACE,{"disambiguationData":[TD([[makeQuery(id+"F0.imprint","IMPRINT",EDGE,{"derivedFrom":sQuery(id+"F0.wireOp",EDGE,"E38")}),1.0]])]});
            var Q5;
            Q5=makeQuery(id+"F0.imprint","IMPRINT",FACE,{"disambiguationData":[TD([[makeQuery(id+"F0.imprint","IMPRINT",EDGE,{"derivedFrom":sQuery(id+"F0.wireOp",EDGE,"E419")}),1.0]])]});
            var Q6;
            Q6=makeQuery(id+"F0.imprint","IMPRINT",FACE,{"disambiguationData":[TD([[makeQuery(id+"F0.imprint","IMPRINT",EDGE,{"derivedFrom":sQuery(id+"F0.wireOp",EDGE,"E433")}),1.0]])]});
            var Q7;
            Q7=makeQuery(id+"F0.imprint","IMPRINT",FACE,{"disambiguationData":[TD([[makeQuery(id+"F0.imprint","IMPRINT",EDGE,{"derivedFrom":sQuery(id+"F0.wireOp",EDGE,"E19")}),1.0]])]});
            var Q8;
            Q8=makeQuery(id+"F0.imprint","IMPRINT",FACE,{"disambiguationData":[TD([[makeQuery(id+"F0.imprint","IMPRINT",EDGE,{"derivedFrom":sQuery(id+"F0.wireOp",EDGE,"E326")}),1.0]])]});
            var Q9;
            Q9=makeQuery(id+"F0.imprint","IMPRINT",FACE,{"disambiguationData":[TD([[makeQuery(id+"F0.imprint","IMPRINT",EDGE,{"derivedFrom":sQuery(id+"F0.wireOp",EDGE,"E13")}),1.0]])]});
            var Q10;
            Q10=makeQuery(id+"F0.imprint","IMPRINT",FACE,{"disambiguationData":[TD([[makeQuery(id+"F0.imprint","IMPRINT",EDGE,{"derivedFrom":sQuery(id+"F0.wireOp",EDGE,"E11")}),1.0]])]});
            var Q11;
            Q11=makeQuery(id+"F0.imprint","IMPRINT",FACE,{"disambiguationData":[TD([[makeQuery(id+"F0.imprint","IMPRINT",EDGE,{"derivedFrom":sQuery(id+"F0.wireOp",EDGE,"E5")}),1.0]])]});
            var Q12;
            Q12=sQuery(id+"F0.wireOp",EDGE,"E237");
            var Q13;
            Q13=sQuery(id+"F0.wireOp",EDGE,"E216");
            var Q14;
            Q14=sQuery(id+"F0.wireOp",EDGE,"E126");
            var Q15;
            Q15=sQuery(id+"F0.wireOp",EDGE,"E226");
            var Q16;
            Q16=sQuery(id+"F0.wireOp",EDGE,"E55");
            var Q17;
            Q17=sQuery(id+"F0.wireOp",EDGE,"E189");
            var Q18;
            Q18=sQuery(id+"F0.wireOp",EDGE,"E121");
            var Q19;
            Q19=sQuery(id+"F0.wireOp",EDGE,"E225");
            var Q20;
            Q20=sQuery(id+"F0.wireOp",EDGE,"E306");
            var Q21;
            Q21=sQuery(id+"F0.wireOp",EDGE,"E145");
            var Q22;
            Q22=sQuery(id+"F0.wireOp",EDGE,"E138");
            var Q23;
            Q23=sQuery(id+"F0.wireOp",EDGE,"E157");
            var Q24;
            Q24=sQuery(id+"F0.wireOp",EDGE,"E278");
            var Q25;
            Q25=sQuery(id+"F0.wireOp",EDGE,"E332");
            var Q26;
            Q26=sQuery(id+"F0.wireOp",EDGE,"E252");
            var Q27;
            Q27=sQuery(id+"F0.wireOp",EDGE,"E77");
            var Q28;
            Q28=sQuery(id+"F0.wireOp",EDGE,"E180");
            var Q29;
            Q29=sQuery(id+"F0.wireOp",EDGE,"E275");
            var Q30;
            Q30=sQuery(id+"F0.wireOp",EDGE,"E127");
            var Q31;
            Q31=sQuery(id+"F0.wireOp",EDGE,"E89");
            var Q32;
            Q32=sQuery(id+"F0.wireOp",EDGE,"E61");
            var Q33;
            Q33=sQuery(id+"F0.wireOp",EDGE,"E231");
            var Q34;
            Q34=sQuery(id+"F0.wireOp",EDGE,"E284");
            var Q35;
            Q35=sQuery(id+"F0.wireOp",EDGE,"E262");
            var Q36;
            Q36=sQuery(id+"F0.wireOp",EDGE,"E238");
            var Q37;
            Q37=sQuery(id+"F0.wireOp",EDGE,"E287");
            var Q38;
            Q38=sQuery(id+"F0.wireOp",EDGE,"E8");
            var Q39;
            Q39=sQuery(id+"F0.wireOp",EDGE,"E52");
            var Q40;
            Q40=sQuery(id+"F0.wireOp",EDGE,"E315");
            var Q41;
            Q41=sQuery(id+"F0.wireOp",EDGE,"E219");
            var Q42;
            Q42=sQuery(id+"F0.wireOp",EDGE,"E449");
            var Q43;
            Q43=sQuery(id+"F0.wireOp",EDGE,"E300");
            var Q44;
            Q44=sQuery(id+"F0.wireOp",EDGE,"E48");
            var Q45;
            Q45=sQuery(id+"F0.wireOp",EDGE,"E297");
            var Q46;
            Q46=sQuery(id+"F0.wireOp",EDGE,"E368");
            var Q47;
            Q47=sQuery(id+"F0.wireOp",EDGE,"E270");
            var Q48;
            Q48=sQuery(id+"F0.wireOp",EDGE,"E463");
            var Q49;
            Q49=sQuery(id+"F0.wireOp",EDGE,"E130");
            var Q50;
            Q50=sQuery(id+"F0.wireOp",EDGE,"E302");
            var Q51;
            Q51=sQuery(id+"F0.wireOp",EDGE,"E285");
            var Q52;
            Q52=sQuery(id+"F0.wireOp",EDGE,"E314");
            var Q53;
            Q53=sQuery(id+"F0.wireOp",EDGE,"E165");
            var Q54;
            Q54=sQuery(id+"F0.wireOp",EDGE,"E457");
            var Q55;
            Q55=sQuery(id+"F0.wireOp",EDGE,"E182");
            var Q56;
            Q56=sQuery(id+"F0.wireOp",EDGE,"E47");
            var Q57;
            Q57=sQuery(id+"F0.wireOp",EDGE,"E266");
            var Q58;
            Q58=sQuery(id+"F0.wireOp",EDGE,"E128");
            var Q59;
            Q59=sQuery(id+"F0.wireOp",EDGE,"E347");
            var Q60;
            Q60=sQuery(id+"F0.wireOp",EDGE,"E191");
            var Q61;
            Q61=sQuery(id+"F0.wireOp",EDGE,"E132");
            var Q62;
            Q62=sQuery(id+"F0.wireOp",EDGE,"E323");
            var Q63;
            Q63=sQuery(id+"F0.wireOp",EDGE,"E214");
            var Q64;
            Q64=sQuery(id+"F0.wireOp",EDGE,"E41");
            var Q65;
            Q65=sQuery(id+"F0.wireOp",EDGE,"E66");
            var Q66;
            Q66=sQuery(id+"F0.wireOp",EDGE,"E281");
            var Q67;
            Q67=sQuery(id+"F0.wireOp",EDGE,"E464");
            var Q68;
            Q68=sQuery(id+"F0.wireOp",EDGE,"E68");
            var Q69;
            Q69=sQuery(id+"F0.wireOp",EDGE,"E470");
            var Q70;
            Q70=sQuery(id+"F0.wireOp",EDGE,"E131");
            var Q71;
            Q71=sQuery(id+"F0.wireOp",EDGE,"E71");
            var Q72;
            Q72=sQuery(id+"F0.wireOp",EDGE,"E163");
            var Q73;
            Q73=sQuery(id+"F0.wireOp",EDGE,"E205");
            var Q74;
            Q74=sQuery(id+"F0.wireOp",EDGE,"E448");
            var Q75;
            Q75=sQuery(id+"F0.wireOp",EDGE,"E236");
            var Q76;
            Q76=sQuery(id+"F0.wireOp",EDGE,"E461");
            var Q77;
            Q77=sQuery(id+"F0.wireOp",EDGE,"E148");
            var Q78;
            Q78=sQuery(id+"F0.wireOp",EDGE,"E147");
            var Q79;
            Q79=sQuery(id+"F0.wireOp",EDGE,"E496");
            var Q80;
            Q80=sQuery(id+"F0.wireOp",EDGE,"E72");
            var Q81;
            Q81=sQuery(id+"F0.wireOp",EDGE,"E386");
            var Q82;
            Q82=sQuery(id+"F0.wireOp",EDGE,"E184");
            var Q83;
            Q83=sQuery(id+"F0.wireOp",EDGE,"E78");
            var Q84;
            Q84=sQuery(id+"F0.wireOp",EDGE,"E179");
            var Q85;
            Q85=sQuery(id+"F0.wireOp",EDGE,"E385");
            var Q86;
            Q86=sQuery(id+"F0.wireOp",EDGE,"E268");
            var Q87;
            Q87=sQuery(id+"F0.wireOp",EDGE,"E161");
            var Q88;
            Q88=sQuery(id+"F0.wireOp",EDGE,"E340");
            var Q89;
            Q89=sQuery(id+"F0.wireOp",EDGE,"E94");
            var Q90;
            Q90=sQuery(id+"F0.wireOp",EDGE,"E220");
            var Q91;
            Q91=sQuery(id+"F0.wireOp",EDGE,"E213");
            var Q92;
            Q92=sQuery(id+"F0.wireOp",EDGE,"E447");
            var Q93;
            Q93=sQuery(id+"F0.wireOp",EDGE,"E339");
            var Q94;
            Q94=sQuery(id+"F0.wireOp",EDGE,"E245");
            var Q95;
            Q95=sQuery(id+"F0.wireOp",EDGE,"E120");
            var Q96;
            Q96=sQuery(id+"F0.wireOp",EDGE,"E257");
            var Q97;
            Q97=sQuery(id+"F0.wireOp",EDGE,"E484");
            var Q98;
            Q98=sQuery(id+"F0.wireOp",EDGE,"E389");
            var Q99;
            Q99=sQuery(id+"F0.wireOp",EDGE,"E460");
            var Q100;
            Q100=sQuery(id+"F0.wireOp",EDGE,"E383");
            var Q101;
            Q101=sQuery(id+"F0.wireOp",EDGE,"E390");
            var Q102;
            Q102=sQuery(id+"F0.wireOp",EDGE,"E312");
            var Q103;
            Q103=sQuery(id+"F0.wireOp",EDGE,"E405");
            var Q104;
            Q104=sQuery(id+"F0.wireOp",EDGE,"E367");
            var Q105;
            Q105=sQuery(id+"F0.wireOp",EDGE,"E325");
            var Q106;
            Q106=sQuery(id+"F0.wireOp",EDGE,"E450");
            var Q107;
            Q107=sQuery(id+"F0.wireOp",EDGE,"E232");
            var Q108;
            Q108=sQuery(id+"F0.wireOp",EDGE,"E272");
            var Q109;
            Q109=sQuery(id+"F0.wireOp",EDGE,"E317");
            var Q110;
            Q110=sQuery(id+"F0.wireOp",EDGE,"E451");
            var Q111;
            Q111=sQuery(id+"F0.wireOp",EDGE,"E267");
            var Q112;
            Q112=sQuery(id+"F0.wireOp",EDGE,"E49");
            var Q113;
            Q113=sQuery(id+"F0.wireOp",EDGE,"E290");
            var Q114;
            Q114=sQuery(id+"F0.wireOp",EDGE,"E303");
            var Q115;
            Q115=sQuery(id+"F0.wireOp",EDGE,"E224");
            var Q116;
            Q116=sQuery(id+"F0.wireOp",EDGE,"E311");
            var Q117;
            Q117=sQuery(id+"F0.wireOp",EDGE,"E469");
            var Q118;
            Q118=sQuery(id+"F0.wireOp",EDGE,"E313");
            var Q119;
            Q119=sQuery(id+"F0.wireOp",EDGE,"E125");
            var Q120;
            Q120=sQuery(id+"F0.wireOp",EDGE,"E310");
            var Q121;
            Q121=sQuery(id+"F0.wireOp",EDGE,"E137");
            var Q122;
            Q122=sQuery(id+"F0.wireOp",EDGE,"E51");
            var Q123;
            Q123=sQuery(id+"F0.wireOp",EDGE,"E206");
            var Q124;
            Q124=sQuery(id+"F0.wireOp",EDGE,"E487");
            var Q125;
            Q125=sQuery(id+"F0.wireOp",EDGE,"E197");
            var Q126;
            Q126=sQuery(id+"F0.wireOp",EDGE,"E188");
            var Q127;
            Q127=sQuery(id+"F0.wireOp",EDGE,"E273");
            var Q128;
            Q128=sQuery(id+"F0.wireOp",EDGE,"E439");
            var Q129;
            Q129=sQuery(id+"F0.wireOp",EDGE,"E379");
            var Q130;
            Q130=sQuery(id+"F0.wireOp",EDGE,"E67");
            var Q131;
            Q131=sQuery(id+"F0.wireOp",EDGE,"E129");
            var Q132;
            Q132=sQuery(id+"F0.wireOp",EDGE,"E54");
            var Q133;
            Q133=sQuery(id+"F0.wireOp",EDGE,"E282");
            var Q134;
            Q134=sQuery(id+"F0.wireOp",EDGE,"E361");
            var Q135;
            Q135=sQuery(id+"F0.wireOp",EDGE,"E319");
            var Q136;
            Q136=sQuery(id+"F0.wireOp",EDGE,"E388");
            var Q137;
            Q137=sQuery(id+"F0.wireOp",EDGE,"E143");
            var Q138;
            Q138=sQuery(id+"F0.wireOp",EDGE,"E359");
            var Q139;
            Q139=sQuery(id+"F0.wireOp",EDGE,"E176");
            var Q140;
            Q140=sQuery(id+"F0.wireOp",EDGE,"E90");
            var Q141;
            Q141=sQuery(id+"F0.wireOp",EDGE,"E459");
            var Q142;
            Q142=sQuery(id+"F0.wireOp",EDGE,"E115");
            var Q143;
            Q143=sQuery(id+"F0.wireOp",EDGE,"E204");
            var Q144;
            Q144=sQuery(id+"F0.wireOp",EDGE,"E230");
            var Q145;
            Q145=sQuery(id+"F0.wireOp",EDGE,"E221");
            var Q146;
            Q146=sQuery(id+"F0.wireOp",EDGE,"E110");
            var Q147;
            Q147=sQuery(id+"F0.wireOp",EDGE,"E468");
            var Q148;
            Q148=sQuery(id+"F0.wireOp",EDGE,"E11");
            var Q149;
            Q149=sQuery(id+"F0.wireOp",EDGE,"E289");
            var Q150;
            Q150=sQuery(id+"F0.wireOp",EDGE,"E346");
            var Q151;
            Q151=sQuery(id+"F0.wireOp",EDGE,"E142");
            var Q152;
            Q152=sQuery(id+"F0.wireOp",EDGE,"E43");
            var Q153;
            Q153=sQuery(id+"F0.wireOp",EDGE,"E414");
            var Q154;
            Q154=sQuery(id+"F0.wireOp",EDGE,"E507");
            var Q155;
            Q155=sQuery(id+"F0.wireOp",EDGE,"E233");
            var Q156;
            Q156=sQuery(id+"F0.wireOp",EDGE,"E271");
            var Q157;
            Q157=sQuery(id+"F0.wireOp",EDGE,"E46");
            var Q158;
            Q158=sQuery(id+"F0.wireOp",EDGE,"E13");
            var Q159;
            Q159=sQuery(id+"F0.wireOp",EDGE,"E509");
            var Q160;
            Q160=sQuery(id+"F0.wireOp",EDGE,"E0");
            var Q161;
            Q161=sQuery(id+"F0.wireOp",EDGE,"E466");
            var Q162;
            Q162=sQuery(id+"F0.wireOp",EDGE,"E365");
            var Q163;
            Q163=sQuery(id+"F0.wireOp",EDGE,"E181");
            var Q164;
            Q164=sQuery(id+"F0.wireOp",EDGE,"E63");
            var Q165;
            Q165=sQuery(id+"F0.wireOp",EDGE,"E353");
            var Q166;
            Q166=sQuery(id+"F0.wireOp",EDGE,"E415");
            var Q167;
            Q167=sQuery(id+"F0.wireOp",EDGE,"E59");
            var Q168;
            Q168=sQuery(id+"F0.wireOp",EDGE,"E504");
            var Q169;
            Q169=sQuery(id+"F0.wireOp",EDGE,"E116");
            var Q170;
            Q170=sQuery(id+"F0.wireOp",EDGE,"E111");
            var Q171;
            Q171=sQuery(id+"F0.wireOp",EDGE,"E467");
            var Q172;
            Q172=sQuery(id+"F0.wireOp",EDGE,"E324");
            var Q173;
            Q173=sQuery(id+"F0.wireOp",EDGE,"E258");
            var Q174;
            Q174=sQuery(id+"F0.wireOp",EDGE,"E295");
            var Q175;
            Q175=sQuery(id+"F0.wireOp",EDGE,"E506");
            var Q176;
            Q176=sQuery(id+"F0.wireOp",EDGE,"E108");
            var Q177;
            Q177=sQuery(id+"F0.wireOp",EDGE,"E21");
            var Q178;
            Q178=sQuery(id+"F0.wireOp",EDGE,"E109");
            var Q179;
            Q179=sQuery(id+"F0.wireOp",EDGE,"E178");
            var Q180;
            Q180=sQuery(id+"F0.wireOp",EDGE,"E490");
            var Q181;
            Q181=sQuery(id+"F0.wireOp",EDGE,"E217");
            var Q182;
            Q182=sQuery(id+"F0.wireOp",EDGE,"E124");
            var Q183;
            Q183=sQuery(id+"F0.wireOp",EDGE,"E364");
            var Q184;
            Q184=sQuery(id+"F0.wireOp",EDGE,"E384");
            var Q185;
            Q185=sQuery(id+"F0.wireOp",EDGE,"E210");
            var Q186;
            Q186=sQuery(id+"F0.wireOp",EDGE,"E434");
            var Q187;
            Q187=sQuery(id+"F0.wireOp",EDGE,"E482");
            var Q188;
            Q188=sQuery(id+"F0.wireOp",EDGE,"E156");
            var Q189;
            Q189=sQuery(id+"F0.wireOp",EDGE,"E452");
            var Q190;
            Q190=sQuery(id+"F0.wireOp",EDGE,"E106");
            var Q191;
            Q191=sQuery(id+"F0.wireOp",EDGE,"E423");
            var Q192;
            Q192=sQuery(id+"F0.wireOp",EDGE,"E123");
            var Q193;
            Q193=sQuery(id+"F0.wireOp",EDGE,"E6");
            var Q194;
            Q194=sQuery(id+"F0.wireOp",EDGE,"E299");
            var Q195;
            Q195=sQuery(id+"F0.wireOp",EDGE,"E69");
            var Q196;
            Q196=sQuery(id+"F0.wireOp",EDGE,"E173");
            var Q197;
            Q197=sQuery(id+"F0.wireOp",EDGE,"E215");
            var Q198;
            Q198=sQuery(id+"F0.wireOp",EDGE,"E87");
            var Q199;
            Q199=sQuery(id+"F0.wireOp",EDGE,"E351");
            var Q200;
            Q200=sQuery(id+"F0.wireOp",EDGE,"E265");
            var Q201;
            Q201=sQuery(id+"F0.wireOp",EDGE,"E472");
            var Q202;
            Q202=sQuery(id+"F0.wireOp",EDGE,"E234");
            var Q203;
            Q203=sQuery(id+"F0.wireOp",EDGE,"E3");
            var Q204;
            Q204=sQuery(id+"F0.wireOp",EDGE,"E29");
            var Q205;
            Q205=sQuery(id+"F0.wireOp",EDGE,"E334");
            var Q206;
            Q206=sQuery(id+"F0.wireOp",EDGE,"E330");
            var Q207;
            Q207=sQuery(id+"F0.wireOp",EDGE,"E307");
            var Q208;
            Q208=sQuery(id+"F0.wireOp",EDGE,"E229");
            var Q209;
            Q209=sQuery(id+"F0.wireOp",EDGE,"E194");
            var Q210;
            Q210=sQuery(id+"F0.wireOp",EDGE,"E169");
            var Q211;
            Q211=sQuery(id+"F0.wireOp",EDGE,"E103");
            var Q212;
            Q212=sQuery(id+"F0.wireOp",EDGE,"E207");
            var Q213;
            Q213=sQuery(id+"F0.wireOp",EDGE,"E403");
            var Q214;
            Q214=sQuery(id+"F0.wireOp",EDGE,"E198");
            var Q215;
            Q215=sQuery(id+"F0.wireOp",EDGE,"E150");
            var Q216;
            Q216=sQuery(id+"F0.wireOp",EDGE,"E80");
            var Q217;
            Q217=sQuery(id+"F0.wireOp",EDGE,"E433");
            var Q218;
            Q218=sQuery(id+"F0.wireOp",EDGE,"E279");
            var Q219;
            Q219=sQuery(id+"F0.wireOp",EDGE,"E159");
            var Q220;
            Q220=sQuery(id+"F0.wireOp",EDGE,"E247");
            var Q221;
            Q221=sQuery(id+"F0.wireOp",EDGE,"E256");
            var Q222;
            Q222=sQuery(id+"F0.wireOp",EDGE,"E316");
            var Q223;
            Q223=sQuery(id+"F0.wireOp",EDGE,"E401");
            var Q224;
            Q224=sQuery(id+"F0.wireOp",EDGE,"E508");
            var Q225;
            Q225=sQuery(id+"F0.wireOp",EDGE,"E305");
            var Q226;
            Q226=sQuery(id+"F0.wireOp",EDGE,"E495");
            var Q227;
            Q227=sQuery(id+"F0.wireOp",EDGE,"E393");
            var Q228;
            Q228=sQuery(id+"F0.wireOp",EDGE,"E481");
            var Q229;
            Q229=sQuery(id+"F0.wireOp",EDGE,"E292");
            var Q230;
            Q230=sQuery(id+"F0.wireOp",EDGE,"E442");
            var Q231;
            Q231=sQuery(id+"F0.wireOp",EDGE,"E357");
            var Q232;
            Q232=sQuery(id+"F0.wireOp",EDGE,"E253");
            var Q233;
            Q233=sQuery(id+"F0.wireOp",EDGE,"E277");
            var Q234;
            Q234=sQuery(id+"F0.wireOp",EDGE,"E491");
            var Q235;
            Q235=sQuery(id+"F0.wireOp",EDGE,"E398");
            var Q236;
            Q236=sQuery(id+"F0.wireOp",EDGE,"E101");
            var Q237;
            Q237=sQuery(id+"F0.wireOp",EDGE,"E274");
            var Q238;
            Q238=sQuery(id+"F0.wireOp",EDGE,"E16");
            var Q239;
            Q239=sQuery(id+"F0.wireOp",EDGE,"E327");
            var Q240;
            Q240=sQuery(id+"F0.wireOp",EDGE,"E12");
            var Q241;
            Q241=sQuery(id+"F0.wireOp",EDGE,"E288");
            var Q242;
            Q242=sQuery(id+"F0.wireOp",EDGE,"E505");
            var Q243;
            Q243=sQuery(id+"F0.wireOp",EDGE,"E140");
            var Q244;
            Q244=sQuery(id+"F0.wireOp",EDGE,"E185");
            var Q245;
            Q245=sQuery(id+"F0.wireOp",EDGE,"E14");
            var Q246;
            Q246=sQuery(id+"F0.wireOp",EDGE,"E366");
            var Q247;
            Q247=sQuery(id+"F0.wireOp",EDGE,"E453");
            var Q248;
            Q248=sQuery(id+"F0.wireOp",EDGE,"E488");
            var Q249;
            Q249=sQuery(id+"F0.wireOp",EDGE,"E374");
            var Q250;
            Q250=sQuery(id+"F0.wireOp",EDGE,"E162");
            var Q251;
            Q251=sQuery(id+"F0.wireOp",EDGE,"E397");
            var Q252;
            Q252=sQuery(id+"F0.wireOp",EDGE,"E411");
            var Q253;
            Q253=sQuery(id+"F0.wireOp",EDGE,"E483");
            var Q254;
            Q254=sQuery(id+"F0.wireOp",EDGE,"E462");
            var Q255;
            Q255=sQuery(id+"F0.wireOp",EDGE,"E510");
            var Q256;
            Q256=sQuery(id+"F0.wireOp",EDGE,"E203");
            var Q257;
            Q257=sQuery(id+"F0.wireOp",EDGE,"E248");
            var Q258;
            Q258=sQuery(id+"F0.wireOp",EDGE,"E352");
            var Q259;
            Q259=sQuery(id+"F0.wireOp",EDGE,"E186");
            var Q260;
            Q260=sQuery(id+"F0.wireOp",EDGE,"E218");
            var Q261;
            Q261=sQuery(id+"F0.wireOp",EDGE,"E387");
            var Q262;
            Q262=sQuery(id+"F0.wireOp",EDGE,"E235");
            var Q263;
            Q263=sQuery(id+"F0.wireOp",EDGE,"E193");
            var Q264;
            Q264=sQuery(id+"F0.wireOp",EDGE,"E22");
            var Q265;
            Q265=sQuery(id+"F0.wireOp",EDGE,"E341");
            var Q266;
            Q266=sQuery(id+"F0.wireOp",EDGE,"E501");
            var Q267;
            Q267=sQuery(id+"F0.wireOp",EDGE,"E465");
            var Q268;
            Q268=sQuery(id+"F0.wireOp",EDGE,"E420");
            var Q269;
            Q269=sQuery(id+"F0.wireOp",EDGE,"E511");
            var Q270;
            Q270=sQuery(id+"F0.wireOp",EDGE,"E190");
            var Q271;
            Q271=sQuery(id+"F0.wireOp",EDGE,"E88");
            var Q272;
            Q272=sQuery(id+"F0.wireOp",EDGE,"E65");
            var Q273;
            Q273=sQuery(id+"F0.wireOp",EDGE,"E454");
            var Q274;
            Q274=sQuery(id+"F0.wireOp",EDGE,"E243");
            var Q275;
            Q275=sQuery(id+"F0.wireOp",EDGE,"E141");
            var Q276;
            Q276=sQuery(id+"F0.wireOp",EDGE,"E438");
            var Q277;
            Q277=sQuery(id+"F0.wireOp",EDGE,"E404");
            var Q278;
            Q278=sQuery(id+"F0.wireOp",EDGE,"E96");
            var Q279;
            Q279=sQuery(id+"F0.wireOp",EDGE,"E342");
            var Q280;
            Q280=sQuery(id+"F0.wireOp",EDGE,"E195");
            var Q281;
            Q281=sQuery(id+"F0.wireOp",EDGE,"E23");
            var Q282;
            Q282=sQuery(id+"F0.wireOp",EDGE,"E74");
            var Q283;
            Q283=sQuery(id+"F0.wireOp",EDGE,"E250");
            var Q284;
            Q284=sQuery(id+"F0.wireOp",EDGE,"E476");
            var Q285;
            Q285=sQuery(id+"F0.wireOp",EDGE,"E280");
            var Q286;
            Q286=sQuery(id+"F0.wireOp",EDGE,"E296");
            var Q287;
            Q287=sQuery(id+"F0.wireOp",EDGE,"E122");
            var Q288;
            Q288=sQuery(id+"F0.wireOp",EDGE,"E320");
            var Q289;
            Q289=sQuery(id+"F0.wireOp",EDGE,"E254");
            var Q290;
            Q290=sQuery(id+"F0.wireOp",EDGE,"E167");
            var Q291;
            Q291=sQuery(id+"F0.wireOp",EDGE,"E458");
            var Q292;
            Q292=sQuery(id+"F0.wireOp",EDGE,"E97");
            var Q293;
            Q293=sQuery(id+"F0.wireOp",EDGE,"E475");
            var Q294;
            Q294=sQuery(id+"F0.wireOp",EDGE,"E139");
            var Q295;
            Q295=sQuery(id+"F0.wireOp",EDGE,"E406");
            var Q296;
            Q296=sQuery(id+"F0.wireOp",EDGE,"E155");
            var Q297;
            Q297=sQuery(id+"F0.wireOp",EDGE,"E298");
            var Q298;
            Q298=sQuery(id+"F0.wireOp",EDGE,"E212");
            var Q299;
            Q299=sQuery(id+"F0.wireOp",EDGE,"E19");
            var Q300;
            Q300=sQuery(id+"F0.wireOp",EDGE,"E144");
            var Q301;
            Q301=sQuery(id+"F0.wireOp",EDGE,"E79");
            var Q302;
            Q302=sQuery(id+"F0.wireOp",EDGE,"E107");
            var Q303;
            Q303=sQuery(id+"F0.wireOp",EDGE,"E441");
            var Q304;
            Q304=sQuery(id+"F0.wireOp",EDGE,"E333");
            var Q305;
            Q305=sQuery(id+"F0.wireOp",EDGE,"E471");
            var Q306;
            Q306=sQuery(id+"F0.wireOp",EDGE,"E269");
            var Q307;
            Q307=sQuery(id+"F0.wireOp",EDGE,"E57");
            var Q308;
            Q308=sQuery(id+"F0.wireOp",EDGE,"E335");
            var Q309;
            Q309=sQuery(id+"F0.wireOp",EDGE,"E242");
            var Q310;
            Q310=sQuery(id+"F0.wireOp",EDGE,"E396");
            var Q311;
            Q311=sQuery(id+"F0.wireOp",EDGE,"E93");
            var Q312;
            Q312=sQuery(id+"F0.wireOp",EDGE,"E175");
            var Q313;
            Q313=sQuery(id+"F0.wireOp",EDGE,"E136");
            var Q314;
            Q314=sQuery(id+"F0.wireOp",EDGE,"E255");
            var Q315;
            Q315=sQuery(id+"F0.wireOp",EDGE,"E177");
            var Q316;
            Q316=sQuery(id+"F0.wireOp",EDGE,"E133");
            var Q317;
            Q317=sQuery(id+"F0.wireOp",EDGE,"E436");
            var Q318;
            Q318=sQuery(id+"F0.wireOp",EDGE,"E192");
            var Q319;
            Q319=sQuery(id+"F0.wireOp",EDGE,"E286");
            var Q320;
            Q320=sQuery(id+"F0.wireOp",EDGE,"E166");
            var Q321;
            Q321=sQuery(id+"F0.wireOp",EDGE,"E209");
            var Q322;
            Q322=sQuery(id+"F0.wireOp",EDGE,"E322");
            var Q323;
            Q323=sQuery(id+"F0.wireOp",EDGE,"E486");
            var Q324;
            Q324=sQuery(id+"F0.wireOp",EDGE,"E413");
            var Q325;
            Q325=sQuery(id+"F0.wireOp",EDGE,"E160");
            var Q326;
            Q326=sQuery(id+"F0.wireOp",EDGE,"E402");
            var Q327;
            Q327=sQuery(id+"F0.wireOp",EDGE,"E489");
            var Q328;
            Q328=sQuery(id+"F0.wireOp",EDGE,"E37");
            var Q329;
            Q329=sQuery(id+"F0.wireOp",EDGE,"E513");
            var Q330;
            Q330=sQuery(id+"F0.wireOp",EDGE,"E363");
            var Q331;
            Q331=sQuery(id+"F0.wireOp",EDGE,"E134");
            var Q332;
            Q332=sQuery(id+"F0.wireOp",EDGE,"E170");
            var Q333;
            Q333=sQuery(id+"F0.wireOp",EDGE,"E418");
            var Q334;
            Q334=sQuery(id+"F0.wireOp",EDGE,"E149");
            var Q335;
            Q335=sQuery(id+"F0.wireOp",EDGE,"E503");
            var Q336;
            Q336=sQuery(id+"F0.wireOp",EDGE,"E208");
            var Q337;
            Q337=sQuery(id+"F0.wireOp",EDGE,"E86");
            var Q338;
            Q338=sQuery(id+"F0.wireOp",EDGE,"E112");
            var Q339;
            Q339=sQuery(id+"F0.wireOp",EDGE,"E222");
            var Q340;
            Q340=sQuery(id+"F0.wireOp",EDGE,"E358");
            var Q341;
            Q341=sQuery(id+"F0.wireOp",EDGE,"E91");
            var Q342;
            Q342=sQuery(id+"F0.wireOp",EDGE,"E400");
            var Q343;
            Q343=sQuery(id+"F0.wireOp",EDGE,"E417");
            var Q344;
            Q344=sQuery(id+"F0.wireOp",EDGE,"E45");
            var Q345;
            Q345=sQuery(id+"F0.wireOp",EDGE,"E168");
            var Q346;
            Q346=sQuery(id+"F0.wireOp",EDGE,"E20");
            var Q347;
            Q347=sQuery(id+"F0.wireOp",EDGE,"E244");
            var Q348;
            Q348=sQuery(id+"F0.wireOp",EDGE,"E5");
            var Q349;
            Q349=sQuery(id+"F0.wireOp",EDGE,"E440");
            var Q350;
            Q350=sQuery(id+"F0.wireOp",EDGE,"E362");
            var Q351;
            Q351=sQuery(id+"F0.wireOp",EDGE,"E64");
            var Q352;
            Q352=sQuery(id+"F0.wireOp",EDGE,"E246");
            var Q353;
            Q353=sQuery(id+"F0.wireOp",EDGE,"E409");
            var Q354;
            Q354=sQuery(id+"F0.wireOp",EDGE,"E337");
            var Q355;
            Q355=sQuery(id+"F0.wireOp",EDGE,"E408");
            var Q356;
            Q356=sQuery(id+"F0.wireOp",EDGE,"E92");
            var Q357;
            Q357=sQuery(id+"F0.wireOp",EDGE,"E117");
            var Q358;
            Q358=sQuery(id+"F0.wireOp",EDGE,"E60");
            var Q359;
            Q359=sQuery(id+"F0.wireOp",EDGE,"E44");
            var Q360;
            Q360=sQuery(id+"F0.wireOp",EDGE,"E308");
            var Q361;
            Q361=sQuery(id+"F0.wireOp",EDGE,"E200");
            var Q362;
            Q362=sQuery(id+"F0.wireOp",EDGE,"E394");
            var Q363;
            Q363=sQuery(id+"F0.wireOp",EDGE,"E171");
            var Q364;
            Q364=sQuery(id+"F0.wireOp",EDGE,"E456");
            var Q365;
            Q365=sQuery(id+"F0.wireOp",EDGE,"E407");
            var Q366;
            Q366=sQuery(id+"F0.wireOp",EDGE,"E421");
            var Q367;
            Q367=sQuery(id+"F0.wireOp",EDGE,"E338");
            var Q368;
            Q368=sQuery(id+"F0.wireOp",EDGE,"E331");
            var Q369;
            Q369=sQuery(id+"F0.wireOp",EDGE,"E480");
            var Q370;
            Q370=sQuery(id+"F0.wireOp",EDGE,"E24");
            var Q371;
            Q371=sQuery(id+"F0.wireOp",EDGE,"E153");
            var Q372;
            Q372=sQuery(id+"F0.wireOp",EDGE,"E512");
            var Q373;
            Q373=sQuery(id+"F0.wireOp",EDGE,"E85");
            var Q374;
            Q374=sQuery(id+"F0.wireOp",EDGE,"E395");
            var Q375;
            Q375=sQuery(id+"F0.wireOp",EDGE,"E381");
            var Q376;
            Q376=sQuery(id+"F0.wireOp",EDGE,"E81");
            var Q377;
            Q377=sQuery(id+"F0.wireOp",EDGE,"E304");
            var Q378;
            Q378=sQuery(id+"F0.wireOp",EDGE,"E371");
            var Q379;
            Q379=sQuery(id+"F0.wireOp",EDGE,"E164");
            var Q380;
            Q380=sQuery(id+"F0.wireOp",EDGE,"E154");
            var Q381;
            Q381=sQuery(id+"F0.wireOp",EDGE,"E326");
            var Q382;
            Q382=sQuery(id+"F0.wireOp",EDGE,"E354");
            var Q383;
            Q383=sQuery(id+"F0.wireOp",EDGE,"E135");
            var Q384;
            Q384=sQuery(id+"F0.wireOp",EDGE,"E318");
            var Q385;
            Q385=sQuery(id+"F0.wireOp",EDGE,"E158");
            var Q386;
            Q386=sQuery(id+"F0.wireOp",EDGE,"E263");
            var Q387;
            Q387=sQuery(id+"F0.wireOp",EDGE,"E146");
            var Q388;
            Q388=sQuery(id+"F0.wireOp",EDGE,"E15");
            var Q389;
            Q389=sQuery(id+"F0.wireOp",EDGE,"E102");
            var Q390;
            Q390=sQuery(id+"F0.wireOp",EDGE,"E416");
            var Q391;
            Q391=sQuery(id+"F0.wireOp",EDGE,"E174");
            var Q392;
            Q392=sQuery(id+"F0.wireOp",EDGE,"E283");
            var Q393;
            Q393=sQuery(id+"F0.wireOp",EDGE,"E301");
            var Q394;
            Q394=sQuery(id+"F0.wireOp",EDGE,"E42");
            var Q395;
            Q395=sQuery(id+"F0.wireOp",EDGE,"E10");
            var Q396;
            Q396=sQuery(id+"F0.wireOp",EDGE,"E1");
            var Q397;
            Q397=sQuery(id+"F0.wireOp",EDGE,"E502");
            var Q398;
            Q398=sQuery(id+"F0.wireOp",EDGE,"E249");
            var Q399;
            Q399=sQuery(id+"F0.wireOp",EDGE,"E240");
            var Q400;
            Q400=sQuery(id+"F0.wireOp",EDGE,"E392");
            var Q401;
            Q401=sQuery(id+"F0.wireOp",EDGE,"E95");
            var Q402;
            Q402=sQuery(id+"F0.wireOp",EDGE,"E239");
            var Q403;
            Q403=sQuery(id+"F0.wireOp",EDGE,"E412");
            var Q404;
            Q404=sQuery(id+"F0.wireOp",EDGE,"E172");
            var Q405;
            Q405=sQuery(id+"F0.wireOp",EDGE,"E196");
            var Q406;
            Q406=sQuery(id+"F0.wireOp",EDGE,"E309");
            var Q407;
            Q407=sQuery(id+"F0.wireOp",EDGE,"E336");
            var Q408;
            Q408=sQuery(id+"F0.wireOp",EDGE,"E151");
            var Q409;
            Q409=sQuery(id+"F0.wireOp",EDGE,"E211");
            var Q410;
            Q410=sQuery(id+"F0.wireOp",EDGE,"E261");
            var Q411;
            Q411=sQuery(id+"F0.wireOp",EDGE,"E382");
            var Q412;
            Q412=sQuery(id+"F0.wireOp",EDGE,"E227");
            var Q413;
            Q413=sQuery(id+"F0.wireOp",EDGE,"E399");
            var Q414;
            Q414=sQuery(id+"F0.wireOp",EDGE,"E294");
            var Q415;
            Q415=sQuery(id+"F0.wireOp",EDGE,"E391");
            var Q416;
            Q416=sQuery(id+"F0.wireOp",EDGE,"E152");
            var Q417;
            Q417=sQuery(id+"F0.wireOp",EDGE,"E329");
            var Q418;
            Q418=sQuery(id+"F0.wireOp",EDGE,"E84");
            var Q419;
            Q419=sQuery(id+"F0.wireOp",EDGE,"E7");
            var Q420;
            Q420=sQuery(id+"F0.wireOp",EDGE,"E32");
            var Q421;
            Q421=sQuery(id+"F0.wireOp",EDGE,"E118");
            var Q422;
            Q422=sQuery(id+"F0.wireOp",EDGE,"E424");
            var Q423;
            Q423=sQuery(id+"F0.wireOp",EDGE,"E479");
            var Q424;
            Q424=sQuery(id+"F0.wireOp",EDGE,"E70");
            var Q425;
            Q425=sQuery(id+"F0.wireOp",EDGE,"E443");
            var Q426;
            Q426=sQuery(id+"F0.wireOp",EDGE,"E328");
            var Q427;
            Q427=sQuery(id+"F0.wireOp",EDGE,"E9");
            var Q428;
            Q428=sQuery(id+"F0.wireOp",EDGE,"E435");
            var Q429;
            Q429=sQuery(id+"F0.wireOp",EDGE,"E31");
            var Q430;
            Q430=sQuery(id+"F0.wireOp",EDGE,"E58");
            var Q431;
            Q431=sQuery(id+"F0.wireOp",EDGE,"E380");
            var Q432;
            Q432=sQuery(id+"F0.wireOp",EDGE,"E360");
            var Q433;
            Q433=sQuery(id+"F0.wireOp",EDGE,"E36");
            var Q434;
            Q434=sQuery(id+"F0.wireOp",EDGE,"E73");
            var Q435;
            Q435=sQuery(id+"F0.wireOp",EDGE,"E455");
            var Q436;
            Q436=sQuery(id+"F0.wireOp",EDGE,"E428");
            var Q437;
            Q437=sQuery(id+"F0.wireOp",EDGE,"E199");
            var Q438;
            Q438=sQuery(id+"F0.wireOp",EDGE,"E355");
            var Q439;
            Q439=sQuery(id+"F0.wireOp",EDGE,"E291");
            var Q440;
            Q440=sQuery(id+"F0.wireOp",EDGE,"E50");
            var Q441;
            Q441=sQuery(id+"F0.wireOp",EDGE,"E497");
            var Q442;
            Q442=sQuery(id+"F0.wireOp",EDGE,"E251");
            var Q443;
            Q443=sQuery(id+"F0.wireOp",EDGE,"E276");
            var Q444;
            Q444=sQuery(id+"F0.wireOp",EDGE,"E241");
            var Q445;
            Q445=sQuery(id+"F0.wireOp",EDGE,"E356");
            var Q446;
            Q446=sQuery(id+"F0.wireOp",EDGE,"E485");
            var Q447;
            Q447=sQuery(id+"F0.wireOp",EDGE,"E56");
            var Q448;
            Q448=sQuery(id+"F0.wireOp",EDGE,"E119");
            var Q449;
            Q449=sQuery(id+"F0.wireOp",EDGE,"E62");
            var Q450;
            Q450=sQuery(id+"F0.wireOp",EDGE,"E53");
            var Q451;
            Q451=sQuery(id+"F0.wireOp",EDGE,"E345");
            var Q452;
            Q452=sQuery(id+"F0.wireOp",EDGE,"E422");
            var Q453;
            Q453=sQuery(id+"F0.wireOp",EDGE,"E113");
            var Q454;
            Q454=sQuery(id+"F0.wireOp",EDGE,"E2");
            var Q455;
            Q455=sQuery(id+"F0.wireOp",EDGE,"E432");
            var Q456;
            Q456=sQuery(id+"F0.wireOp",EDGE,"E26");
            var Q457;
            Q457=sQuery(id+"F0.wireOp",EDGE,"E373");
            var Q458;
            Q458=sQuery(id+"F0.wireOp",EDGE,"E499");
            var Q459;
            Q459=sQuery(id+"F0.wireOp",EDGE,"E228");
            var Q460;
            Q460=sQuery(id+"F0.wireOp",EDGE,"E187");
            var Q461;
            Q461=sQuery(id+"F0.wireOp",EDGE,"E114");
            var Q462;
            Q462=sQuery(id+"F0.wireOp",EDGE,"E17");
            var Q463;
            Q463=sQuery(id+"F0.wireOp",EDGE,"E493");
            var Q464;
            Q464=sQuery(id+"F0.wireOp",EDGE,"E369");
            var Q465;
            Q465=sQuery(id+"F0.wireOp",EDGE,"E477");
            var Q466;
            Q466=sQuery(id+"F0.wireOp",EDGE,"E372");
            var Q467;
            Q467=sQuery(id+"F0.wireOp",EDGE,"E444");
            var Q468;
            Q468=sQuery(id+"F0.wireOp",EDGE,"E264");
            var Q469;
            Q469=sQuery(id+"F0.wireOp",EDGE,"E419");
            var Q470;
            Q470=sQuery(id+"F0.wireOp",EDGE,"E474");
            var Q471;
            Q471=sQuery(id+"F0.wireOp",EDGE,"E183");
            var Q472;
            Q472=sQuery(id+"F0.wireOp",EDGE,"E437");
            var Q473;
            Q473=sQuery(id+"F0.wireOp",EDGE,"E321");
            var Q474;
            Q474=sQuery(id+"F0.wireOp",EDGE,"E375");
            var Q475;
            Q475=sQuery(id+"F0.wireOp",EDGE,"E492");
            var Q476;
            Q476=sQuery(id+"F0.wireOp",EDGE,"E104");
            var Q477;
            Q477=sQuery(id+"F0.wireOp",EDGE,"E446");
            var Q478;
            Q478=sQuery(id+"F0.wireOp",EDGE,"E431");
            var Q479;
            Q479=sQuery(id+"F0.wireOp",EDGE,"E38");
            var Q480;
            Q480=sQuery(id+"F0.wireOp",EDGE,"E83");
            var Q481;
            Q481=sQuery(id+"F0.wireOp",EDGE,"E494");
            var Q482;
            Q482=sQuery(id+"F0.wireOp",EDGE,"E223");
            var Q483;
            Q483=sQuery(id+"F0.wireOp",EDGE,"E98");
            var Q484;
            Q484=sQuery(id+"F0.wireOp",EDGE,"E39");
            var Q485;
            Q485=sQuery(id+"F0.wireOp",EDGE,"E445");
            var Q486;
            Q486=sQuery(id+"F0.wireOp",EDGE,"E376");
            var Q487;
            Q487=sQuery(id+"F0.wireOp",EDGE,"E370");
            var Q488;
            Q488=sQuery(id+"F0.wireOp",EDGE,"E473");
            var Q489;
            Q489=sQuery(id+"F0.wireOp",EDGE,"E25");
            var Q490;
            Q490=sQuery(id+"F0.wireOp",EDGE,"E18");
            var Q491;
            Q491=sQuery(id+"F0.wireOp",EDGE,"E478");
            var Q492;
            Q492=sQuery(id+"F0.wireOp",EDGE,"E82");
            var Q493;
            Q493=sQuery(id+"F0.wireOp",EDGE,"E500");
            var Q494;
            Q494=sQuery(id+"F0.wireOp",EDGE,"E40");
            var Q495;
            Q495=sQuery(id+"F0.wireOp",EDGE,"E429");
            var Q496;
            Q496=sQuery(id+"F0.wireOp",EDGE,"E99");
            var Q497;
            Q497=sQuery(id+"F0.wireOp",EDGE,"E343");
            var Q498;
            Q498=sQuery(id+"F0.wireOp",EDGE,"E430");
            var Q499;
            Q499=sQuery(id+"F0.wireOp",EDGE,"E410");
            var Q500;
            Q500=sQuery(id+"F0.wireOp",EDGE,"E27");
            var Q501;
            Q501=sQuery(id+"F0.wireOp",EDGE,"E34");
            var Q502;
            Q502=sQuery(id+"F0.wireOp",EDGE,"E201");
            var Q503;
            Q503=sQuery(id+"F0.wireOp",EDGE,"E202");
            var Q504;
            Q504=sQuery(id+"F0.wireOp",EDGE,"E498");
            var Q505;
            Q505=sQuery(id+"F0.wireOp",EDGE,"E293");
            var Q506;
            Q506=sQuery(id+"F0.wireOp",EDGE,"E260");
            var Q507;
            Q507=sQuery(id+"F0.wireOp",EDGE,"E348");
            var Q508;
            Q508=sQuery(id+"F0.wireOp",EDGE,"E30");
            var Q509;
            Q509=sQuery(id+"F0.wireOp",EDGE,"E378");
            var Q510;
            Q510=sQuery(id+"F0.wireOp",EDGE,"E377");
            var Q511;
            Q511=sQuery(id+"F0.wireOp",EDGE,"E427");
            var Q512;
            Q512=sQuery(id+"F0.wireOp",EDGE,"E259");
            var Q513;
            Q513=sQuery(id+"F0.wireOp",EDGE,"E28");
            var Q514;
            Q514=sQuery(id+"F0.wireOp",EDGE,"E426");
            var Q515;
            Q515=sQuery(id+"F0.wireOp",EDGE,"E33");
            var Q516;
            Q516=sQuery(id+"F0.wireOp",EDGE,"E100");
            var Q517;
            Q517=sQuery(id+"F0.wireOp",EDGE,"E105");
            var Q518;
            Q518=sQuery(id+"F0.wireOp",EDGE,"E425");
            var Q519;
            Q519=sQuery(id+"F0.wireOp",EDGE,"E344");
            var Q520;
            Q520=sQuery(id+"F0.wireOp",EDGE,"E76");
            var Q521;
            Q521=sQuery(id+"F0.wireOp",EDGE,"E350");
            var Q522;
            Q522=sQuery(id+"F0.wireOp",EDGE,"E35");
            var Q523;
            Q523=sQuery(id+"F0.wireOp",EDGE,"E349");
            var Q524;
            Q524=sQuery(id+"F0.wireOp",EDGE,"E75");
            var Q525;
            Q525=sQuery(id+"F0.wireOp",EDGE,"E4");
            extrude(context, id + "F1", {"entities" : qUnion([Q0, Q1, Q2, Q3, Q4, Q5, Q6, Q7, Q8, Q9, Q10, Q11]), "surfaceEntities" : qUnion([Q12, Q13, Q14, Q15, Q16, Q17, Q18, Q19, Q20, Q21, Q22, Q23, Q24, Q25, Q26, Q27, Q28, Q29, Q30, Q31, Q32, Q33, Q34, Q35, Q36, Q37, Q38, Q39, Q40, Q41, Q42, Q43, Q44, Q45, Q46, Q47, Q48, Q49, Q50, Q51, Q52, Q53, Q54, Q55, Q56, Q57, Q58, Q59, Q60, Q61, Q62, Q63, Q64, Q65, Q66, Q67, Q68, Q69, Q70, Q71, Q72, Q73, Q74, Q75, Q76, Q77, Q78, Q79, Q80, Q81, Q82, Q83, Q84, Q85, Q86, Q87, Q88, Q89, Q90, Q91, Q92, Q93, Q94, Q95, Q96, Q97, Q98, Q99, Q100, Q101, Q102, Q103, Q104, Q105, Q106, Q107, Q108, Q109, Q110, Q111, Q112, Q113, Q114, Q115, Q116, Q117, Q118, Q119, Q120, Q121, Q122, Q123, Q124, Q125, Q126, Q127, Q128, Q129, Q130, Q131, Q132, Q133, Q134, Q135, Q136, Q137, Q138, Q139, Q140, Q141, Q142, Q143, Q144, Q145, Q146, Q147, Q148, Q149, Q150, Q151, Q152, Q153, Q154, Q155, Q156, Q157, Q158, Q159, Q160, Q161, Q162, Q163, Q164, Q165, Q166, Q167, Q168, Q169, Q170, Q171, Q172, Q173, Q174, Q175, Q176, Q177, Q178, Q179, Q180, Q181, Q182, Q183, Q184, Q185, Q186, Q187, Q188, Q189, Q190, Q191, Q192, Q193, Q194, Q195, Q196, Q197, Q198, Q199, Q200, Q201, Q202, Q203, Q204, Q205, Q206, Q207, Q208, Q209, Q210, Q211, Q212, Q213, Q214, Q215, Q216, Q217, Q218, Q219, Q220, Q221, Q222, Q223, Q224, Q225, Q226, Q227, Q228, Q229, Q230, Q231, Q232, Q233, Q234, Q235, Q236, Q237, Q238, Q239, Q240, Q241, Q242, Q243, Q244, Q245, Q246, Q247, Q248, Q249, Q250, Q251, Q252, Q253, Q254, Q255, Q256, Q257, Q258, Q259, Q260, Q261, Q262, Q263, Q264, Q265, Q266, Q267, Q268, Q269, Q270, Q271, Q272, Q273, Q274, Q275, Q276, Q277, Q278, Q279, Q280, Q281, Q282, Q283, Q284, Q285, Q286, Q287, Q288, Q289, Q290, Q291, Q292, Q293, Q294, Q295, Q296, Q297, Q298, Q299, Q300, Q301, Q302, Q303, Q304, Q305, Q306, Q307, Q308, Q309, Q310, Q311, Q312, Q313, Q314, Q315, Q316, Q317, Q318, Q319, Q320, Q321, Q322, Q323, Q324, Q325, Q326, Q327, Q328, Q329, Q330, Q331, Q332, Q333, Q334, Q335, Q336, Q337, Q338, Q339, Q340, Q341, Q342, Q343, Q344, Q345, Q346, Q347, Q348, Q349, Q350, Q351, Q352, Q353, Q354, Q355, Q356, Q357, Q358, Q359, Q360, Q361, Q362, Q363, Q364, Q365, Q366, Q367, Q368, Q369, Q370, Q371, Q372, Q373, Q374, Q375, Q376, Q377, Q378, Q379, Q380, Q381, Q382, Q383, Q384, Q385, Q386, Q387, Q388, Q389, Q390, Q391, Q392, Q393, Q394, Q395, Q396, Q397, Q398, Q399, Q400, Q401, Q402, Q403, Q404, Q405, Q406, Q407, Q408, Q409, Q410, Q411, Q412, Q413, Q414, Q415, Q416, Q417, Q418, Q419, Q420, Q421, Q422, Q423, Q424, Q425, Q426, Q427, Q428, Q429, Q430, Q431, Q432, Q433, Q434, Q435, Q436, Q437, Q438, Q439, Q440, Q441, Q442, Q443, Q444, Q445, Q446, Q447, Q448, Q449, Q450, Q451, Q452, Q453, Q454, Q455, Q456, Q457, Q458, Q459, Q460, Q461, Q462, Q463, Q464, Q465, Q466, Q467, Q468, Q469, Q470, Q471, Q472, Q473, Q474, Q475, Q476, Q477, Q478, Q479, Q480, Q481, Q482, Q483, Q484, Q485, Q486, Q487, Q488, Q489, Q490, Q491, Q492, Q493, Q494, Q495, Q496, Q497, Q498, Q499, Q500, Q501, Q502, Q503, Q504, Q505, Q506, Q507, Q508, Q509, Q510, Q511, Q512, Q513, Q514, Q515, Q516, Q517, Q518, Q519, Q520, Q521, Q522, Q523, Q524, Q525]), "depth" : 2 * mm, "offsetDistance" : 25 * mm});
        }
        {
            var Q0;
            Q0 = qSketchRegion(id + "F0", true);
            var Q1;
            Q1=makeQuery(id+"F0.imprint","IMPRINT",FACE,{"disambiguationData":[TD([[makeQuery(id+"F0.imprint","IMPRINT",EDGE,{"derivedFrom":sQuery(id+"F0.wireOp",EDGE,"E34")}),-1.0]])]});
            extrude(context, id + "F2", {"entities" : qUnion([Q0, Q1]), "operationType" : NewBodyOperationType.ADD, "depth" : 3 * mm, "offsetDistance" : 25 * mm});
        }
    });
